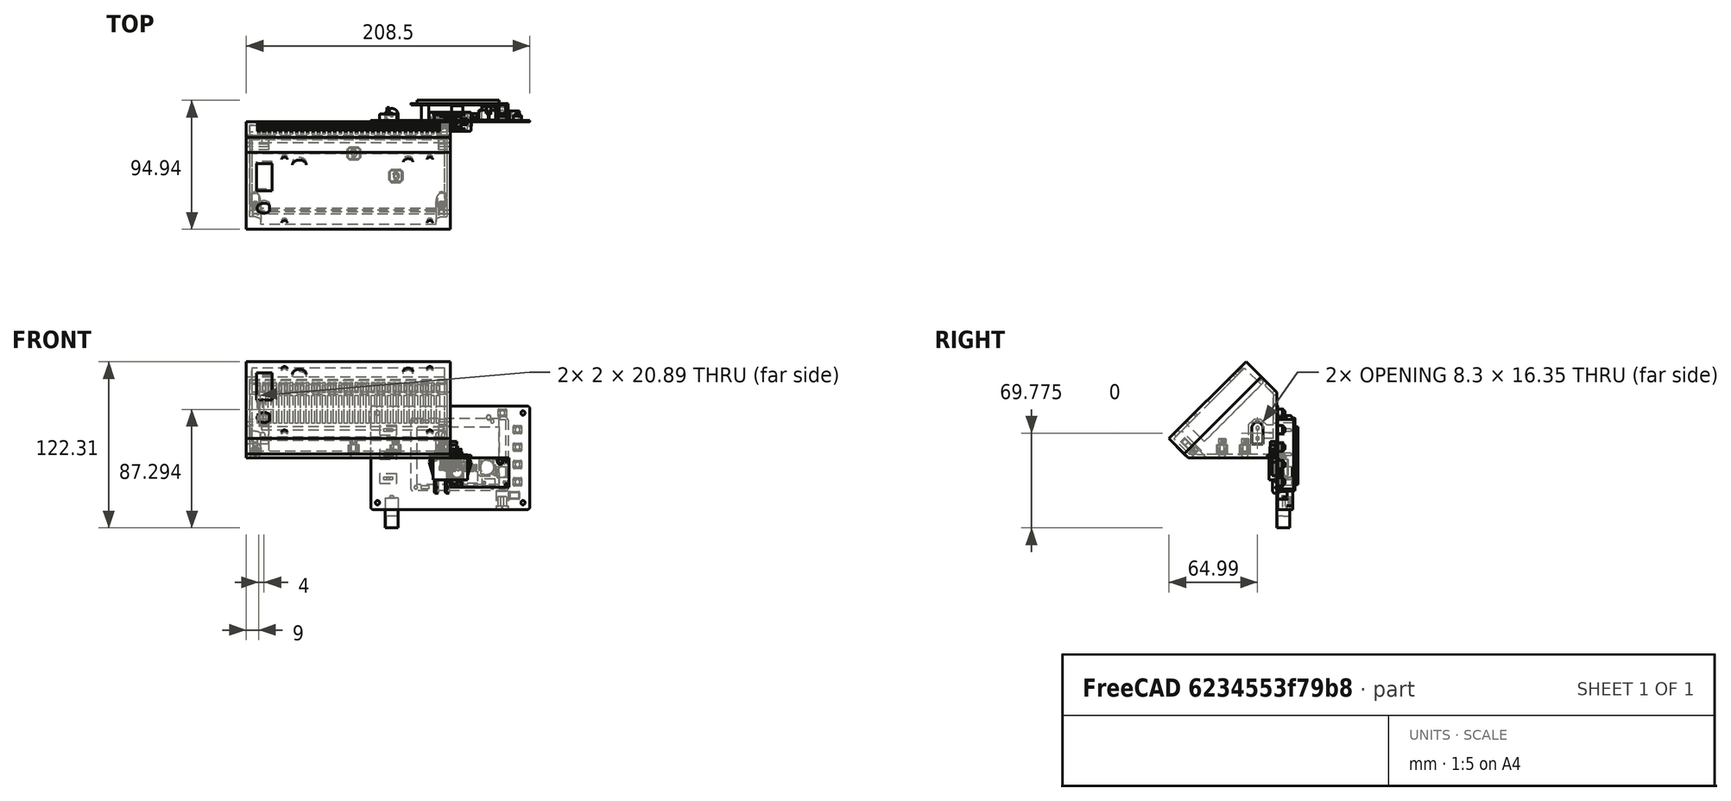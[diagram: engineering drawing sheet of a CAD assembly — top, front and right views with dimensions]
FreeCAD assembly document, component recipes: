
FREECAD ASSEMBLY — COMPONENT RECIPES ("oscillo_009_surBase35mm_007.5")

This assembly document has 19 components, labeled P0..P18 below (a component is one placed body or linked part). 12 of them carry a construction recipe — the FreeCAD feature program that regenerates the part from scratch, quoted from this document or its linked companion documents; the rest are supplied as boundary geometry only. No exploded tour is included for this assembly.
COMPONENT P0 — recipe-attached ("base", modeled in this document).
Construction recipe (the document's own serialized feature program — sketch geometry with constraints, then the solid features built on it; lengths are millimeters unless a unit is written):

FEATURE [PartDesign::FeatureBase] Clone
  BaseFeature = -> Slice_child0
FEATURE [PartDesign::Thickness] Thickness
  Base = -> Clone [Face7]
  BaseFeature = -> Clone
  Intersection = false
  Join = 0
  Mode = 0
  Reversed = true
  SupportTransform = false
  Value = 2.5
  expr: Value = <<sp>>.epaisseurParois
FEATURE [PartDesign::Plane] DatumPlane001  label="planXt"
  AttachmentOffset = pos=(0,0,-2.5) rot=(0,0,1;0rad)
  Length = 110.737
  MapMode = 5
  Placement = pos=(-2.5,6e-16,-6e-16) rot=(0.57735,0.57735,0.57735;2.0944rad)
  ResizeMode = 0
  Support = -> [YZ_Plane002]
  Width = 102.305
  expr: .AttachmentOffset.Base.z = -<<sp>>.epaisseurParois
FEATURE [Sketcher::SketchObject] Sketch002  label="sk_renfortXt"
  FullyConstrained = true
  MapMode = 5
  Placement = pos=(-2.5,6e-16,-6e-16) rot=(0.57735,0.57735,0.57735;2.0944rad)
  Support = -> [DatumPlane001]
  expr: .Constraints.dist = <<sp>>.xt60distanceAngleBord
  expr: .Constraints.epRf = <<sp>>.xt60epRenfort
  expr: Constraints[13] = <<sp>>.xt60largeurFetiere
  expr: Constraints[14] = <<sp>>.xt60hauteur
  expr: Constraints[15] = <<sp>>.xt60hauteurToit
  expr: Constraints[16] = <<sp>>.xt60base
  expr: Constraints[18] = .Constraints.dist
  expr: Constraints[31] = <<sp>>.epaisseurParois
  expr: Constraints[32] = .Constraints.epRf
  expr: Constraints[34] = .Constraints.epRf
  expr: Constraints[45] = <<sp>>.epaisseurParois
  sketch-geometry (17):
    g0: LineSegment StartX=-18.3 StartY=10 StartZ=0 EndX=-18.3 EndY=23.25 EndZ=0
    g1: LineSegment StartX=-18.3 StartY=23.25 StartZ=0 EndX=-15.65 EndY=25.75 EndZ=0
    g2: LineSegment StartX=-15.65 StartY=25.75 StartZ=0 EndX=-12.65 EndY=25.75 EndZ=0
    g3: LineSegment StartX=-12.65 StartY=25.75 StartZ=0 EndX=-10 EndY=23.25 EndZ=0
    g4: LineSegment StartX=-10 StartY=23.25 StartZ=0 EndX=-10 EndY=10 EndZ=0
    g5: LineSegment StartX=-10 StartY=10 StartZ=0 EndX=-18.3 EndY=10 EndZ=0
    g6: LineSegment StartX=-14.15 StartY=10 StartZ=0 EndX=-14.15 EndY=25.75 EndZ=0
    g7: LineSegment StartX=-16.6431 StartY=28.25 StartZ=0 EndX=-20.8 EndY=24.3284 EndZ=0
    g8: LineSegment StartX=-20.8 StartY=24.3284 StartZ=0 EndX=-20.8 EndY=2.5 EndZ=0
    g9: LineSegment StartX=-20.8 StartY=2.5 StartZ=0 EndX=-7.5 EndY=2.5 EndZ=0
    g10: LineSegment StartX=-7.5 StartY=2.5 StartZ=0 EndX=-7.5 EndY=24.3284 EndZ=0
    g11: LineSegment StartX=-7.5 StartY=24.3284 StartZ=0 EndX=-11.6569 EndY=28.25 EndZ=0
    g12: LineSegment StartX=-11.6569 StartY=28.25 StartZ=0 EndX=-16.6431 EndY=28.25 EndZ=0
    g13: LineSegment StartX=-7.5 StartY=24.3284 StartZ=0 EndX=-2.5 EndY=24.3284 EndZ=0
    g14: LineSegment StartX=-2.5 StartY=24.3284 StartZ=0 EndX=-2.5 EndY=2.5 EndZ=0
    g15: LineSegment StartX=-2.5 StartY=2.5 StartZ=0 EndX=-7.5 EndY=2.5 EndZ=0
    g16: LineSegment StartX=-7.5 StartY=2.5 StartZ=0 EndX=-7.5 EndY=24.3284 EndZ=0
  constraints (46):
    c: Vertical(g0)
    c: Coincident(g0,g1)
    c: Coincident(g1,g2)
    c: Horizontal(g2)
    c: Coincident(g2,g3)
    c: Coincident(g3,g4)
    c: Vertical(g4)
    c: Coincident(g4,g5)
    c: Coincident(g5,g0)
    c: Horizontal(g5)
    c: Symmetric(g1,g2,g6)
    c: Equal(g0,g4)
    c: Symmetric(g0,g4,g6)
    c: DistanceX(g2,g2) = 3
    c: DistanceY(g4,g4) = 13.25
    c: DistanceY(g3,g2) = 2.5
    c: DistanceX(g5,g5) = 8.3
    c: DistanceX(g4,g-1) = 10  'dist'
    c: DistanceY(g-1,g4) = 10
    c: Coincident(g7,g8)
    c: Vertical(g8)
    c: Coincident(g8,g9)
    c: Horizontal(g9)
    c: Coincident(g9,g10)
    c: Coincident(g10,g11)
    c: Coincident(g11,g12)
    c: Coincident(g12,g7)
    c: Symmetric(g7,g10,g6)
    c: Symmetric(g7,g11,g6)
    c: Symmetric(g8,g9,g6)
    c: DistanceX(g8,g0) = 2.5  'epRf'
    c: DistanceY(g-1,g9) = 2.5
    c: Distance(g7,g1) = 2.5
    c: Parallel(g1,g7)
    c: DistanceY(g2,g11) = 2.5
    c: Coincident(g13,g14)
    c: Coincident(g14,g15)
    c: Coincident(g15,g16)
    c: Coincident(g16,g13)
    c: Horizontal(g13)
    c: Horizontal(g15)
    c: Vertical(g14)
    c: Vertical(g16)
    c: Coincident(g13,g11)
    c: Horizontal(g14,g9)
    c: DistanceX(g14,g-1) = 2.5
FEATURE [PartDesign::Pad] Pad001  label="renfortXt"
  AllowMultiFace = false
  BaseFeature = -> Thickness
  Direction = (1,1,1)
  Length = 145
  Length2 = 100
  Profile = -> Sketch002
  Reversed = true
  Type = 0
  expr: Length = <<sp>>.largeurModuleBase - 2 * <<sp>>.epaisseurParois
FEATURE [Sketcher::SketchObject] Sketch003  label="sk_trouXt"
  FullyConstrained = true
  MapMode = 5
  Placement = pos=(0,0,0) rot=(0.57735,0.57735,0.57735;2.0944rad)
  Support = -> [YZ_Plane002]
  expr: .Constraints.dist = <<sp>>.xt60distanceAngleBord
  expr: Constraints[13] = <<sp>>.xt60base
  expr: Constraints[14] = <<sp>>.xt60hauteur
  expr: Constraints[15] = <<sp>>.xt60hauteurToit + <<sp>>.xtJeu
  expr: Constraints[16] = <<sp>>.xt60largeurFetiere
  expr: Constraints[18] = .Constraints.dist
  sketch-geometry (7):
    g0: LineSegment StartX=-18.3 StartY=10 StartZ=0 EndX=-18.3 EndY=23.25 EndZ=0
    g1: LineSegment StartX=-18.3 StartY=23.25 StartZ=0 EndX=-15.65 EndY=26.35 EndZ=0
    g2: LineSegment StartX=-15.65 StartY=26.35 StartZ=0 EndX=-12.65 EndY=26.35 EndZ=0
    g3: LineSegment StartX=-12.65 StartY=26.35 StartZ=0 EndX=-10 EndY=23.25 EndZ=0
    g4: LineSegment StartX=-10 StartY=23.25 StartZ=0 EndX=-10 EndY=10 EndZ=0
    g5: LineSegment StartX=-10 StartY=10 StartZ=0 EndX=-18.3 EndY=10 EndZ=0
    g6: LineSegment StartX=-14.15 StartY=10 StartZ=0 EndX=-14.15 EndY=26.35 EndZ=0
  constraints (19):
    c: Vertical(g0)
    c: Coincident(g0,g1)
    c: Coincident(g1,g2)
    c: Horizontal(g2)
    c: Coincident(g2,g3)
    c: Coincident(g3,g4)
    c: Coincident(g4,g5)
    c: Coincident(g5,g0)
    c: Horizontal(g5)
    c: Symmetric(g1,g2,g6)
    c: Symmetric(g0,g3,g6)
    c: Vertical(g6)
    c: Symmetric(g0,g4,g6)
    c: DistanceX(g5,g5) = 8.3
    c: DistanceY(g4,g4) = 13.25
    c: DistanceY(g3,g2) = 3.1
    c: DistanceX(g2,g2) = 3
    c: DistanceX(g4,g-1) = 10  'dist'
    c: DistanceY(g-1,g4) = 10
FEATURE [PartDesign::Pocket] Pocket
  AllowMultiFace = false
  BaseFeature = -> Pad001
  Direction = (1,1,1)
  Length = 150
  Length2 = 100
  Profile = -> Sketch003
  Type = 0
  expr: Length = <<sp>>.largeurModuleBase
FEATURE [PartDesign::Plane] DatumPlane002  label="planDecoupeRenfortXt"
  AttachmentOffset = pos=(0,0,2.5) rot=(0,0,1;0rad)
  Length = 199.331
  MapMode = 5
  Placement = pos=(0,-2.5,-6e-16) rot=(1,0,0;1.5708rad)
  ResizeMode = 0
  Support = -> [XZ_Plane002]
  Width = 108.899
  expr: .AttachmentOffset.Base.z = <<sp>>.epaisseurParois
FEATURE [Sketcher::SketchObject] Sketch004  label="sk_decoupRenfXt"
  FullyConstrained = true
  MapMode = 5
  Placement = pos=(0,-2.5,-6e-16) rot=(1,0,0;1.5708rad)
  Support = -> [DatumPlane002]
  expr: Constraints[10] = <<sp>>.xt60LongueurRenfortPetit + <<sp>>.epaisseurParois
  expr: Constraints[11] = <<sp>>.largeurModuleBase - (<<sp>>.xt60longueurRenfortGrand + <<sp>>.epaisseurParois)
  expr: Constraints[8] = <<sp>>.epaisseurParois
  expr: Constraints[9] = <<sp>>.xt60distanceAngleBord + <<sp>>.xt60hauteur + <<sp>>.xt60hauteurToit + <<sp>>.xt60epRenfort
  sketch-geometry (4):
    g0: LineSegment StartX=-133.5 StartY=28.25 StartZ=0 EndX=-8.5 EndY=28.25 EndZ=0
    g1: LineSegment StartX=-8.5 StartY=28.25 StartZ=0 EndX=-8.5 EndY=2.5 EndZ=0
    g2: LineSegment StartX=-8.5 StartY=2.5 StartZ=0 EndX=-133.5 EndY=2.5 EndZ=0
    g3: LineSegment StartX=-133.5 StartY=2.5 StartZ=0 EndX=-133.5 EndY=28.25 EndZ=0
  constraints (12):
    c: Coincident(g0,g1)
    c: Coincident(g1,g2)
    c: Coincident(g2,g3)
    c: Coincident(g3,g0)
    c: Horizontal(g0)
    c: Horizontal(g2)
    c: Vertical(g1)
    c: Vertical(g3)
    c: DistanceY(g-1,g1) = 2.5
    c: DistanceY(g-1,g0) = 28.25
    c: DistanceX(g1,g-1) = 8.5
    c: DistanceX(g2,g-1) = 133.5
FEATURE [PartDesign::Pocket] Pocket001  label="decoupeRenfXt"
  AllowMultiFace = false
  BaseFeature = -> Pocket
  Direction = (1,1,1)
  Length = 23.3
  Length2 = 100
  Profile = -> Sketch004
  Reversed = true
  Type = 0
  expr: Length = <<sp>>.xt60distanceAngleBord + <<sp>>.xt60base + 2 * <<sp>>.xt60epRenfort
FEATURE [Sketcher::SketchObject] Sketch005  label="xt60PercagePostMale"
  FullyConstrained = true
  MapMode = 5
  Placement = pos=(0,0,0) rot=(1,0,0;1.5708rad)
  Support = -> [XZ_Plane002]
  expr: Constraints[0] = <<sp>>.insertDiamPercage
  expr: Constraints[1] = <<sp>>.insertDistanceTrouBordMale
  expr: Constraints[2] = <<sp>>.insertHauteur
  sketch-geometry (1):
    g0: Circle CenterX=-4.5 CenterY=16.625 CenterZ=0 NormalX=0 NormalY=0 NormalZ=1 AngleXU=0 Radius=2
  constraints (3):
    c: Diameter(g0) = 4
    c: DistanceX(g0,g-1) = 4.5
    c: DistanceY(g-1,g0) = 16.625
FEATURE [PartDesign::Pocket] Pocket002  label="insertXtMale"
  AllowMultiFace = false
  BaseFeature = -> Pocket001
  Direction = (1,1,1)
  Length = 10
  Length2 = 100
  Profile = -> Sketch005
  Reversed = true
  Type = 0
  expr: Length = <<sp>>.insertProfondeurPercage
FEATURE [Sketcher::SketchObject] Sketch006  label="xt60PercagePostFem"
  FullyConstrained = true
  MapMode = 5
  Placement = pos=(0,0,0) rot=(1,0,0;1.5708rad)
  Support = -> [XZ_Plane002]
  expr: Constraints[0] = <<sp>>.insertDiamPercage
  expr: Constraints[1] = <<sp>>.insertDistanceTrouBordFem
  expr: Constraints[2] = <<sp>>.insertHauteur
  sketch-geometry (1):
    g0: Circle CenterX=-138 CenterY=16.625 CenterZ=0 NormalX=0 NormalY=0 NormalZ=1 AngleXU=0 Radius=2
  constraints (3):
    c: Diameter(g0) = 4
    c: DistanceX(g0,g-1) = 138
    c: DistanceY(g-1,g0) = 16.625
FEATURE [PartDesign::Pocket] Pocket003  label="insertXt60Fem"
  AllowMultiFace = false
  BaseFeature = -> Pocket002
  Direction = (1,1,1)
  Length = 10
  Length2 = 100
  Profile = -> Sketch006
  Reversed = true
  Type = 0
  expr: Length = <<sp>>.insertProfondeurPercage
FEATURE [PartDesign::Plane] DatumPlane003
  AttachmentOffset = pos=(0,0,2.5) rot=(0,0,1;0rad)
  Length = 200.515
  MapMode = 2
  Placement = pos=(0,0,2.5) rot=(0,0,1;0rad)
  ResizeMode = 0
  Support = -> [XY_Plane002]
  Width = 118.515
  expr: .AttachmentOffset.Base.z = <<sp>>.epaisseurParois
FEATURE [PartDesign::Plane] DatumPlane004  label="planTrancheur"
  AttachmentOffset = pos=(0,0,71) rot=(-1,0,0;0.785398rad)
  Length = 204.647
  MapMode = 5
  Placement = pos=(0,-71,-1.58e-14) rot=(1,0,0;0.785398rad)
  ResizeMode = 0
  Support = -> [XZ_Plane002]
  Width = 155.206
  expr: .AttachmentOffset.Base.z = <<sp>>.planTrancheur
FEATURE [Sketcher::SketchObject] Sketch008
  FullyConstrained = true
  MapMode = 5
  Placement = pos=(0,-71,-2.13e-14) rot=(1,0,0;0.785398rad)
  Support = -> [DatumPlane004]
  expr: .Constraints.dist = <<sp>>.epaisseurParois
  expr: Constraints[13] = <<sp>>.epaisseurParois
  expr: Constraints[16] = <<sp>>.insertDiamPercage / 2 + <<sp>>.insertFAVMargeDist
  expr: Constraints[1] = <<sp>>.insertFavDistAuZeroDuPLan
  expr: Constraints[21] = <<sp>>.insertFAVDistBord
  expr: Constraints[22] = <<sp>>.largeurModuleBase - <<sp>>.epaisseurParois
  sketch-geometry (7):
    g0: LineSegment StartX=-2.5 StartY=4.24264 StartZ=0 EndX=-147.5 EndY=4.24264 EndZ=0
    g1: LineSegment StartX=-6.5 StartY=14.7426 StartZ=0 EndX=-2.5 EndY=14.7426 EndZ=0
    g2: LineSegment StartX=-2.5 StartY=14.7426 StartZ=0 EndX=-2.5 EndY=6.74264 EndZ=0
    g3: LineSegment StartX=-2.5 StartY=6.74264 StartZ=0 EndX=-10.5 EndY=6.74264 EndZ=0
    g4: LineSegment StartX=-10.5 StartY=6.74264 StartZ=0 EndX=-10.5 EndY=10.7426 EndZ=0
    g5: ArcOfCircle CenterX=-6.5 CenterY=10.7426 CenterZ=0 NormalX=0 NormalY=0 NormalZ=1 AngleXU=0 Radius=4 StartAngle=1.5708 EndAngle=3.14159
    g6: LineSegment StartX=-6.5 StartY=10.7426 StartZ=0 EndX=-6.5 EndY=6.74264 EndZ=0
  constraints (23):
    c: Horizontal(g0)
    c: DistanceY(g-1,g0) = 4.24264
    c: DistanceX(g0,g-1) = 2.5  'dist'
    c: Horizontal(g1)
    c: Coincident(g1,g2)
    c: Vertical(g2)
    c: Coincident(g2,g3)
    c: Horizontal(g3)
    c: Coincident(g3,g4)
    c: Vertical(g4)
    c: Vertical(g2,g0)
    c: Equal(g3,g2)
    c: Equal(g4,g1)
    c: DistanceY(g0,g2) = 2.5
    c: Coincident(g5,g4)
    c: Coincident(g5,g1)
    c: DistanceX(g5,g2) = 4
    c: Coincident(g6,g5)
    c: PointOnObject(g6,g3)
    c: Vertical(g6)
    c: Vertical(g5,g1)
    c: DistanceX(g3,g3) = 8
    c: DistanceX(g0,g-1) = 147.5
FEATURE [PartDesign::Pad] Pad003  label="padTrouFAVDroite"
  AllowMultiFace = false
  BaseFeature = -> Pocket003
  Direction = (1,1,1)
  Length = 10
  Length2 = 100
  Profile = -> Sketch008
  Reversed = true
  Type = 3
  UpToFace = -> DatumPlane003
FEATURE [Sketcher::SketchObject] Sketch009
  FullyConstrained = true
  MapMode = 5
  Placement = pos=(0,-71,-2.13e-14) rot=(1,0,0;0.785398rad)
  Support = -> [DatumPlane004]
  expr: .Constraints.larg = <<sp>>.insertFAVDistBord
  expr: Constraints[11] = .Constraints.larg / 2
  expr: Constraints[12] = <<sp>>.largeurModuleBase
  expr: Constraints[13] = <<sp>>.insertFavDistAuZeroDuPLan
  expr: Constraints[14] = <<sp>>.epaisseurParois
  expr: Constraints[15] = <<sp>>.epaisseurParois
  expr: Constraints[8] = .Constraints.larg
  sketch-geometry (6):
    g0: LineSegment StartX=-147.5 StartY=6.74264 StartZ=0 EndX=-139.5 EndY=6.74264 EndZ=0
    g1: LineSegment StartX=-139.5 StartY=6.74264 StartZ=0 EndX=-139.5 EndY=10.7426 EndZ=0
    g2: LineSegment StartX=-143.5 StartY=14.7426 StartZ=0 EndX=-147.5 EndY=14.7426 EndZ=0
    g3: LineSegment StartX=-147.5 StartY=14.7426 StartZ=0 EndX=-147.5 EndY=6.74264 EndZ=0
    g4: ArcOfCircle CenterX=-143.5 CenterY=10.7426 CenterZ=0 NormalX=0 NormalY=0 NormalZ=1 AngleXU=0 Radius=4 StartAngle=0 EndAngle=1.5708
    g5: GeomPoint X=-150 Y=4.24264 Z=0
  constraints (16):
    c: Coincident(g0,g1)
    c: Coincident(g2,g3)
    c: Coincident(g3,g0)
    c: Horizontal(g0)
    c: Horizontal(g2)
    c: Vertical(g1)
    c: Vertical(g3)
    c: DistanceX(g0,g0) = 8  'larg'
    c: DistanceY(g3,g3) = 8
    c: Tangent(g2,g4) = -1.5708
    c: Tangent(g1,g4) = -1.5708
    c: DistanceX(g0,g4) = 4
    c: DistanceX(g5,g-1) = 150
    c: DistanceY(g-1,g5) = 4.24264
    c: DistanceX(g5,g0) = 2.5
    c: DistanceY(g5,g0) = 2.5
FEATURE [PartDesign::Pad] Pad004  label="padTrouFavGauche"
  AllowMultiFace = false
  BaseFeature = -> Pad003
  Direction = (1,1,1)
  Length = 10
  Length2 = 100
  Profile = -> Sketch009
  Type = 3
  UpToFace = -> DatumPlane003 [Plane]
FEATURE [Sketcher::SketchObject] Sketch010
  FullyConstrained = true
  MapMode = 5
  Placement = pos=(0,-71,-2.13e-14) rot=(1,0,0;0.785398rad)
  Support = -> [DatumPlane004]
  expr: Constraints[0] = <<sp>>.insertFAVDistBord / 2 + <<sp>>.epaisseurParois
  expr: Constraints[1] = <<sp>>.insertFavDistAuZeroDuPLan + <<sp>>.epaisseurParois + <<sp>>.insertFAVDistBord / 2
  expr: Constraints[2] = <<sp>>.insertDiamPercage
  sketch-geometry (1):
    g0: Circle CenterX=-6.5 CenterY=10.7426 CenterZ=0 NormalX=0 NormalY=0 NormalZ=1 AngleXU=0 Radius=2
  constraints (3):
    c: DistanceX(g0,g-1) = 6.5
    c: DistanceY(g-1,g0) = 10.7426
    c: Diameter(g0) = 4
FEATURE [PartDesign::Pocket] Pocket004  label="trouDroit"
  AllowMultiFace = false
  BaseFeature = -> Pad004
  Direction = (1,1,1)
  Length = 5
  Length2 = 100
  Profile = -> Sketch010
  Type = 1
FEATURE [Sketcher::SketchObject] Sketch011
  FullyConstrained = true
  MapMode = 5
  Placement = pos=(0,-71,-2.13e-14) rot=(1,0,0;0.785398rad)
  Support = -> [DatumPlane004]
  expr: Constraints[0] = <<sp>>.insertDiamPercage
  expr: Constraints[1] = <<sp>>.largeurModuleBase - <<sp>>.epaisseurParois - <<sp>>.insertFAVDistBord / 2
  expr: Constraints[2] = <<sp>>.insertFavDistAuZeroDuPLan + <<sp>>.epaisseurParois + <<sp>>.insertFAVDistBord / 2
  sketch-geometry (1):
    g0: Circle CenterX=-143.5 CenterY=10.7426 CenterZ=0 NormalX=0 NormalY=0 NormalZ=1 AngleXU=0 Radius=2
  constraints (3):
    c: Diameter(g0) = 4
    c: DistanceX(g0,g-1) = 143.5
    c: DistanceY(g-1,g0) = 10.7426
FEATURE [PartDesign::Pocket] Pocket005  label="trouGauche"
  AllowMultiFace = false
  BaseFeature = -> Pocket004
  Direction = (1,1,1)
  Length = 5
  Length2 = 100
  Profile = -> Sketch011
  Type = 1
FEATURE [PartDesign::Plane] DatumPlane005  label="planTeteVisFav"
  AttachmentOffset = pos=(0,0,68) rot=(-1,0,0;0.785398rad)
  Length = 204.647
  MapMode = 5
  Placement = pos=(0,-68,-1.51e-14) rot=(1,0,0;0.785398rad)
  ResizeMode = 0
  Support = -> [XZ_Plane002]
  Width = 155.206
  expr: .AttachmentOffset.Base.z = <<sp>>.planTrancheur - 3
FEATURE [Sketcher::SketchObject] Sketch012
  ExternalGeometry = -> [Pocket005]
  FullyConstrained = true
  MapMode = 5
  Placement = pos=(0,-68,-1.42e-14) rot=(1,0,0;0.785398rad)
  Support = -> [DatumPlane005]
  expr: Constraints[1] = <<sp>>.visM3DiamEncastrement
  sketch-geometry (2):
    g0: Circle CenterX=-6.5 CenterY=8.62132 CenterZ=0 NormalX=0 NormalY=0 NormalZ=1 AngleXU=0 Radius=3
    g1: Circle CenterX=-143.5 CenterY=8.62132 CenterZ=0 NormalX=0 NormalY=0 NormalZ=1 AngleXU=0 Radius=3
  constraints (4):
    c: Equal(g0,g1)
    c: Diameter(g1) = 6
    c: Coincident(g1,g-4)
    c: Coincident(g-3,g0)
FEATURE [PartDesign::Pocket] Pocket006  label="evidementTeteVisFav"
  AllowMultiFace = false
  BaseFeature = -> Pocket005
  Direction = (1,1,1)
  Length = 20
  Length2 = 100
  Profile = -> Sketch012
  Type = 1
FEATURE [Sketcher::SketchObject] Sketch014
  FullyConstrained = true
  MapMode = 5
  Placement = pos=(0,0,0) rot=(1,0,0;1.5708rad)
  Support = -> [XZ_Plane002]
  expr: Constraints[12] = <<sp>>.xt60distanceAngleBord + <<sp>>.xt60hauteur + <<sp>>.ventilDistBordFente
  expr: Constraints[13] = <<sp>>.ventilLargeurFentes
  expr: Constraints[14] = <<sp>>.ventilEcartfente / 2
  expr: Constraints[15] = <<sp>>.hauteurDuDos - <<sp>>.ventilDistBordFente
  expr: Constraints[2] = <<sp>>.hauteurDuDos
  expr: Constraints[3] = <<sp>>.largeurModuleBase / 2
  sketch-geometry (5):
    g0: LineSegment StartX=-75 StartY=0 StartZ=0 EndX=-75 EndY=48.1371 EndZ=0
    g1: LineSegment StartX=-78 StartY=46.1371 StartZ=0 EndX=-76 EndY=46.1371 EndZ=0
    g2: LineSegment StartX=-76 StartY=46.1371 StartZ=0 EndX=-76 EndY=25.25 EndZ=0
    g3: LineSegment StartX=-76 StartY=25.25 StartZ=0 EndX=-78 EndY=25.25 EndZ=0
    g4: LineSegment StartX=-78 StartY=25.25 StartZ=0 EndX=-78 EndY=46.1371 EndZ=0
  constraints (16):
    c: PointOnObject(g0,g-1)
    c: Vertical(g0)
    c: DistanceY(g0,g0) = 48.1371
    c: DistanceX(g0,g-1) = 75
    c: Coincident(g1,g2)
    c: Coincident(g2,g3)
    c: Coincident(g3,g4)
    c: Coincident(g4,g1)
    c: Horizontal(g1)
    c: Horizontal(g3)
    c: Vertical(g2)
    c: Vertical(g4)
    c: DistanceY(g-1,g2) = 25.25
    c: DistanceX(g1,g1) = 2
    c: DistanceX(g2,g0) = 1
    c: DistanceY(g-1,g1) = 46.1371
FEATURE [PartDesign::Pocket] Pocket008  label="ventilFente1"
  AllowMultiFace = false
  BaseFeature = -> Pocket006
  Direction = (1,1,1)
  Length = 2.5
  Length2 = 100
  Profile = -> Sketch014
  Reversed = true
  Type = 0
  expr: Length = <<sp>>.epaisseurParois
FEATURE [PartDesign::LinearPattern] LinearPattern  label="ventilDosRepeat1"
  BaseFeature = -> Pocket008
  Direction = -> Sketch014 [H_Axis]
  Length = 64
  Occurrences = 17
  Originals = -> [Pocket008]
  Reversed = true
  expr: Length = <<sp>>.ventilLargeurRepet
  expr: Occurrences = <<sp>>.ventilNbrFents
FEATURE [PartDesign::LinearPattern] LinearPattern001  label="ventilDosRepeat2"
  BaseFeature = -> LinearPattern
  Direction = -> Sketch014 [H_Axis]
  Length = 68
  Occurrences = 18
  Originals = -> [Pocket008]
  expr: Length = <<sp>>.ventilLargeurRepet + <<sp>>.ventilEcartfente + <<sp>>.ventilLargeurFentes
  expr: Occurrences = <<sp>>.ventilNbrFents + 1
FEATURE [PartDesign::Plane] DatumPlane006  label="planVentilSup"
  AttachmentOffset = pos=(0,0,-48.1371) rot=(1,0,0;0.785398rad)
  Length = 204.647
  MapMode = 5
  Placement = pos=(0,48.1371,1.07e-14) rot=(1,0,0;2.35619rad)
  ResizeMode = 0
  Support = -> [XZ_Plane002]
  Width = 155.206
  expr: .AttachmentOffset.Base.z = -<<sp>>.hauteurDuDos
FEATURE [Sketcher::SketchObject] Sketch015
  FullyConstrained = true
  MapMode = 5
  Placement = pos=(0,48.1371,1.07e-14) rot=(1,0,0;2.35619rad)
  Support = -> [DatumPlane006]
  expr: Constraints[10] = <<sp>>.ventilLargeurFentes
  expr: Constraints[11] = (<<sp>>.largeurModuleBase + <<sp>>.ventilEcartfente) / 2
  expr: Constraints[8] = <<sp>>.distanceAuZeroPlanBorArriere + <<sp>>.ventilDistBordFente
  expr: Constraints[9] = <<sp>>.longPetitRetSupSansFav - 2 * <<sp>>.ventilDistBordFente - <<sp>>.favBordureProf
  sketch-geometry (4):
    g0: LineSegment StartX=-76 StartY=78.0926 StartZ=0 EndX=-78 EndY=78.0926 EndZ=0
    g1: LineSegment StartX=-78 StartY=78.0926 StartZ=0 EndX=-78 EndY=70.0761 EndZ=0
    g2: LineSegment StartX=-78 StartY=70.0761 StartZ=0 EndX=-76 EndY=70.0761 EndZ=0
    g3: LineSegment StartX=-76 StartY=70.0761 StartZ=0 EndX=-76 EndY=78.0926 EndZ=0
  constraints (12):
    c: Coincident(g0,g1)
    c: Coincident(g1,g2)
    c: Coincident(g2,g3)
    c: Coincident(g3,g0)
    c: Horizontal(g0)
    c: Horizontal(g2)
    c: Vertical(g1)
    c: Vertical(g3)
    c: DistanceY(g-1,g2) = 70.0761
    c: DistanceY(g2,g0) = 8.01652
    c: DistanceX(g0,g0) = 2
    c: DistanceX(g2,g-1) = 76
FEATURE [PartDesign::Pocket] Pocket009  label="ventilSupFente"
  AllowMultiFace = false
  BaseFeature = -> LinearPattern001
  Direction = (1,1,1)
  Length = 5
  Length2 = 100
  Profile = -> Sketch015
  Reversed = true
  Type = 0
FEATURE [PartDesign::LinearPattern] LinearPattern002  label="ventilSupRepeat1"
  BaseFeature = -> Pocket009
  Direction = -> Sketch015 [H_Axis]
  Length = 64
  Occurrences = 17
  Originals = -> [Pocket009]
  Reversed = true
  expr: Length = <<sp>>.ventilLargeurRepet
  expr: Occurrences = <<sp>>.ventilNbrFents
FEATURE [PartDesign::LinearPattern] LinearPattern003  label="ventilSupRepeat2"
  BaseFeature = -> LinearPattern002
  Direction = -> Sketch015 [H_Axis]
  Length = 68
  Occurrences = 18
  Originals = -> [Pocket009]
  expr: Length = <<sp>>.ventilLargeurRepet + <<sp>>.ventilEcartfente + <<sp>>.ventilLargeurFentes
  expr: Occurrences = <<sp>>.ventilNbrFents + 1
FEATURE [PartDesign::Body] Body001  label="base"
  BaseFeature = -> Slice_child0
  Group = -> [Clone,Thickness,DatumPlane001,Sketch002,Pad001,Sketch003,Pocket,DatumPlane002,Sketch004,Pocket001,Sketch005,Pocket002,Sketch006,Pocket003,DatumPlane003,DatumPlane004,Sketch008,Pad003,Sketch009,Pad004,Sketch010,Pocket004,Sketch011,Pocket005,DatumPlane005,Sketch012,Pocket006,Sketch014,Pocket008,LinearPattern,LinearPattern001,DatumPlane006,Sketch015,Pocket009,LinearPattern002,LinearPattern003,+10 more]
  Origin = -> Origin002
  Tip = -> Chamfer005
COMPONENT P1 — recipe-attached ("faceAvant", modeled in this document).
Construction recipe (the document's own serialized feature program — sketch geometry with constraints, then the solid features built on it; lengths are millimeters unless a unit is written):

FEATURE [PartDesign::FeatureBase] Clone001
  BaseFeature = -> Slice_child1
FEATURE [PartDesign::Thickness] Thickness001
  Base = -> Clone001 [Face5]
  BaseFeature = -> Clone001
  Intersection = false
  Join = 0
  Mode = 0
  Reversed = true
  SupportTransform = false
  Value = 2.5
  expr: Value = <<sp>>.epaisseurParois
FEATURE [PartDesign::Plane] DatumPlane007  label="planTrancheurBis"
  AttachmentOffset = pos=(0,0,71) rot=(-1,0,0;0.785398rad)
  Length = 206.452
  MapMode = 5
  Placement = pos=(0,-71,-1.58e-14) rot=(1,0,0;0.785398rad)
  ResizeMode = 0
  Support = -> [XZ_Plane003]
  Width = 172.769
  expr: .AttachmentOffset.Base.z = <<sp>>.planTrancheur
FEATURE [Sketcher::SketchObject] Sketch016  label="sk_insertFavDroit"
  FullyConstrained = true
  MapMode = 5
  Placement = pos=(0,-71,-2.13e-14) rot=(1,0,0;0.785398rad)
  Support = -> [DatumPlane007]
  expr: Constraints[11] = <<sp>>.insertFAVDistBord
  expr: Constraints[14] = <<sp>>.insertFAVDistBord / 2
  expr: Constraints[7] = <<sp>>.epaisseurParois
  expr: Constraints[8] = <<sp>>.insertFavDistAuZeroDuPLan + <<sp>>.epaisseurParois
  expr: Constraints[9] = <<sp>>.insertFAVDistBord
  sketch-geometry (5):
    g0: LineSegment StartX=-6.5 StartY=14.7426 StartZ=0 EndX=-2.5 EndY=14.7426 EndZ=0
    g1: LineSegment StartX=-2.5 StartY=14.7426 StartZ=0 EndX=-2.5 EndY=6.74264 EndZ=0
    g2: LineSegment StartX=-2.5 StartY=6.74264 StartZ=0 EndX=-10.5 EndY=6.74264 EndZ=0
    g3: LineSegment StartX=-10.5 StartY=6.74264 StartZ=0 EndX=-10.5 EndY=10.7426 EndZ=0
    g4: ArcOfCircle CenterX=-6.5 CenterY=10.7426 CenterZ=0 NormalX=0 NormalY=0 NormalZ=1 AngleXU=0 Radius=4 StartAngle=1.5708 EndAngle=3.14159
  constraints (15):
    c: Horizontal(g0)
    c: Coincident(g0,g1)
    c: Vertical(g1)
    c: Coincident(g1,g2)
    c: Horizontal(g2)
    c: Coincident(g2,g3)
    c: Vertical(g3)
    c: DistanceX(g1,g-1) = 2.5
    c: DistanceY(g-1,g1) = 6.74264
    c: DistanceY(g1,g1) = 8
    c: Equal(g3,g0)
    c: DistanceX(g2,g2) = 8
    c: Coincident(g4,g0)
    c: Tangent(g4,g3) = 1.5708
    c: DistanceX(g4,g1) = 4
FEATURE [PartDesign::Pad] Pad005  label="padInsertFavDroit"
  AllowMultiFace = false
  BaseFeature = -> Thickness001
  Direction = (1,1,1)
  Length = 10
  Length2 = 100
  Profile = -> Sketch016
  Type = 2
FEATURE [Sketcher::SketchObject] Sketch017  label="sp_padInserFavGauch"
  FullyConstrained = true
  MapMode = 5
  Placement = pos=(0,-71,-2.13e-14) rot=(1,0,0;0.785398rad)
  Support = -> [DatumPlane007]
  expr: Constraints[10] = <<sp>>.insertFAVDistBord
  expr: Constraints[12] = <<sp>>.insertFAVDistBord / 2
  expr: Constraints[13] = <<sp>>.largeurModuleBase
  expr: Constraints[14] = <<sp>>.insertFavDistAuZeroDuPLan
  expr: Constraints[15] = <<sp>>.epaisseurParois
  expr: Constraints[16] = <<sp>>.epaisseurParois
  sketch-geometry (6):
    g0: LineSegment StartX=-143.5 StartY=14.7426 StartZ=0 EndX=-147.5 EndY=14.7426 EndZ=0
    g1: LineSegment StartX=-147.5 StartY=14.7426 StartZ=0 EndX=-147.5 EndY=6.74264 EndZ=0
    g2: LineSegment StartX=-147.5 StartY=6.74264 StartZ=0 EndX=-139.5 EndY=6.74264 EndZ=0
    g3: LineSegment StartX=-139.5 StartY=6.74264 StartZ=0 EndX=-139.5 EndY=10.7426 EndZ=0
    g4: ArcOfCircle CenterX=-143.5 CenterY=10.7426 CenterZ=0 NormalX=0 NormalY=0 NormalZ=1 AngleXU=0 Radius=4 StartAngle=0 EndAngle=1.5708
    g5: GeomPoint X=-150 Y=4.24264 Z=0
  constraints (17):
    c: Horizontal(g0)
    c: Coincident(g0,g1)
    c: Vertical(g1)
    c: Coincident(g1,g2)
    c: Horizontal(g2)
    c: Coincident(g2,g3)
    c: Vertical(g3)
    c: Equal(g3,g0)
    c: Equal(g2,g1)
    c: Coincident(g0,g4)
    c: DistanceX(g2,g2) = 8
    c: Tangent(g4,g3) = -1.5708
    c: DistanceX(g0,g0) = 4
    c: DistanceX(g5,g-1) = 150
    c: DistanceY(g-1,g5) = 4.24264
    c: DistanceY(g5,g1) = 2.5
    c: DistanceX(g5,g1) = 2.5
FEATURE [PartDesign::Pad] Pad006  label="padInsertFavGauch"
  AllowMultiFace = false
  BaseFeature = -> Pad005
  Direction = (1,1,1)
  Length = 10
  Length2 = 100
  Profile = -> Sketch017
  Type = 2
FEATURE [Sketcher::SketchObject] Sketch018  label="skPercageInsertFavDroit"
  FullyConstrained = true
  MapMode = 5
  Placement = pos=(0,-71,-2.13e-14) rot=(1,0,0;0.785398rad)
  Support = -> [DatumPlane007]
  expr: Constraints[0] = <<sp>>.insertDiamPercage
  expr: Constraints[1] = <<sp>>.insertFavDistAuZeroDuPLan + <<sp>>.epaisseurParois + <<sp>>.insertFAVDistBord / 2
  expr: Constraints[2] = <<sp>>.epaisseurParois + <<sp>>.insertFAVDistBord / 2
  expr: Constraints[7] = <<sp>>.largeurModuleBase - 2 * <<sp>>.epaisseurParois - <<sp>>.insertFAVDistBord
  sketch-geometry (3):
    g0: Circle CenterX=-6.5 CenterY=10.7426 CenterZ=0 NormalX=0 NormalY=0 NormalZ=1 AngleXU=0 Radius=2
    g1: Circle CenterX=-143.5 CenterY=10.7426 CenterZ=0 NormalX=0 NormalY=0 NormalZ=1 AngleXU=0 Radius=2
    g2: LineSegment StartX=-143.5 StartY=10.7426 StartZ=0 EndX=-6.5 EndY=10.7426 EndZ=0
  constraints (8):
    c: Diameter(g0) = 4
    c: DistanceY(g-1,g0) = 10.7426
    c: DistanceX(g0,g-1) = 6.5
    c: Equal(g0,g1)
    c: Coincident(g2,g1)
    c: Coincident(g2,g0)
    c: Horizontal(g2)
    c: DistanceX(g2,g2) = 137
FEATURE [PartDesign::Pocket] Pocket010  label="trouInsertFavDroit"
  AllowMultiFace = false
  BaseFeature = -> Pad006
  Direction = (1,1,1)
  Length = 8
  Length2 = 100
  Profile = -> Sketch018
  Reversed = true
  Type = 0
  expr: Length = <<sp>>.insertFavProfondeur
FEATURE [PartDesign::Plane] DatumPlane011  label="planFaceAvant"
  AttachmentOffset = pos=(0,0,93.2843) rot=(-1,0,0;0.785398rad)
  Length = 206.452
  MapMode = 5
  Placement = pos=(0,-93.2843,-2.07e-14) rot=(1,0,0;0.785398rad)
  ResizeMode = 0
  Support = -> [XZ_Plane003]
  Width = 172.769
  expr: .AttachmentOffset.Base.z = <<sp>>.planFaceAvant
FEATURE [Sketcher::SketchObject] Sketch030  label="sk_rebordFav"
  FullyConstrained = true
  MapMode = 5
  Placement = pos=(0,-71,-2.13e-14) rot=(1,0,0;0.785398rad)
  Support = -> [DatumPlane007]
  expr: Constraints[0] = <<sp>>.insertFavDistAuZeroDuPLan
  expr: Constraints[19] = <<sp>>.epaisseurParois
  expr: Constraints[20] = <<sp>>.favEpBordure
  expr: Constraints[21] = <<sp>>.favDistBordPlan
  expr: Constraints[22] = <<sp>>.largeurModuleBase - 2 * <<sp>>.epaisseurParois
  expr: Constraints[23] = <<sp>>.favEpBordure
  expr: Constraints[24] = <<sp>>.Face - <<sp>>.epaisseurParois
  expr: Constraints[25] = <<sp>>.favEpBordure
  sketch-geometry (9):
    g0: GeomPoint X=0 Y=4.24264 Z=0
    g1: LineSegment StartX=-147.5 StartY=20.9853 StartZ=0 EndX=-147.5 EndY=81.7426 EndZ=0
    g2: LineSegment StartX=-147.5 StartY=81.7426 StartZ=0 EndX=-2.5 EndY=81.7426 EndZ=0
    g3: LineSegment StartX=-2.5 StartY=81.7426 StartZ=0 EndX=-2.5 EndY=20.9853 EndZ=0
    g4: LineSegment StartX=-2.5 StartY=20.9853 StartZ=0 EndX=-4 EndY=20.9853 EndZ=0
    g5: LineSegment StartX=-4 StartY=20.9853 StartZ=0 EndX=-4 EndY=80.2426 EndZ=0
    g6: LineSegment StartX=-4 StartY=80.2426 StartZ=0 EndX=-146 EndY=80.2426 EndZ=0
    g7: LineSegment StartX=-146 StartY=80.2426 StartZ=0 EndX=-146 EndY=20.9853 EndZ=0
    g8: LineSegment StartX=-146 StartY=20.9853 StartZ=0 EndX=-147.5 EndY=20.9853 EndZ=0
  constraints (26):
    c: DistanceY(g-1,g0) = 4.24264
    c: Vertical(g0,g-1)
    c: Vertical(g1)
    c: Coincident(g1,g2)
    c: Horizontal(g2)
    c: Coincident(g2,g3)
    c: Vertical(g3)
    c: Coincident(g3,g4)
    c: Horizontal(g4)
    c: Coincident(g4,g5)
    c: Vertical(g5)
    c: Coincident(g5,g6)
    c: Horizontal(g6)
    c: Coincident(g6,g7)
    c: Vertical(g7)
    c: Coincident(g7,g8)
    c: Coincident(g8,g1)
    c: Horizontal(g8)
    c: Horizontal(g7,g4)
    c: DistanceX(g3,g0) = 2.5
    c: DistanceX(g4,g4) = 1.5
    c: DistanceY(g0,g3) = 16.7426
    c: DistanceX(g1,g3) = 145
    c: DistanceY(g5,g2) = 1.5
    c: DistanceY(g0,g2) = 77.5
    c: DistanceX(g1,g7) = 1.5
FEATURE [PartDesign::Pad] Pad014  label="favRebordSupport"
  AllowMultiFace = false
  BaseFeature = -> Pocket010
  Direction = (1,1,1)
  Length = 10
  Length2 = 100
  Profile = -> Sketch030
  Type = 3
  UpToFace = -> Pocket010 [Face13]
FEATURE [PartDesign::Pad] Pad015  label="favRebord"
  AllowMultiFace = false
  BaseFeature = -> Pad014
  Direction = (1,1,1)
  Length = 4.15
  Length2 = 100
  Profile = -> Sketch030
  Reversed = true
  Type = 0
  expr: Length = <<sp>>.favBordureProf
FEATURE [Sketcher::SketchObject] Sketch031  label="sk_bourlet"
  ExternalGeometry = -> [Pad015]
  FullyConstrained = true
  MapMode = 5
  Placement = pos=(-2.5,0,0) rot=(0.57735,0.57735,0.57735;2.0944rad)
  Support = -> [Pad015]
  expr: Constraints[3] = <<sp>>.bourletMaintientRayon - <<sp>>.bourletRayonJeu
  sketch-geometry (2):
    g0: ArcOfCircle CenterX=-11.184 CenterY=55.7855 CenterZ=0 NormalX=0 NormalY=0 NormalZ=1 AngleXU=0 Radius=1.3 StartAngle=5.49779 EndAngle=8.63938
    g1: LineSegment StartX=-12.1032 StartY=56.7048 StartZ=0 EndX=-10.2647 EndY=54.8663 EndZ=0
  constraints (6):
    c: Coincident(g0,g-3)
    c: PointOnObject(g0,g-3)
    c: PointOnObject(g0,g-3)
    c: Radius(g0) = 1.3
    c: Coincident(g1,g0)
    c: Coincident(g1,g0)
FEATURE [PartDesign::Pad] Pad016  label="bourlet"
  AllowMultiFace = false
  BaseFeature = -> Pad015
  Direction = (1,1,1)
  Length = 10
  Length2 = 100
  Profile = -> Sketch031
  Reversed = true
  Type = 3
  UpToFace = -> Pad015 [Face11]
FEATURE [Sketcher::SketchObject] Sketch034  label="favTrous001"
  FullyConstrained = true
  MapMode = 5
  Placement = pos=(0,-93.2843,-2.84e-14) rot=(1,0,0;0.785398rad)
  Support = -> [DatumPlane011]
  expr: Constraints[10] = <<sp>>.distZeroPlanFAV
  expr: Constraints[12] = <<favTrous>>.switchPosX
  expr: Constraints[13] = <<favTrous>>.switchPosY
  expr: Constraints[27] = <<favTrous>>.oscilloDistTrousX
  expr: Constraints[28] = <<favTrous>>.oscilloTrouDiam
  expr: Constraints[29] = <<favTrous>>.oscilloDistTrousY
  expr: Constraints[30] = <<favTrous>>.oscilloTrou1PosX
  expr: Constraints[31] = <<favTrous>>.oscilloTrou1PosY
  expr: Constraints[8] = <<SW_C1500AT>>.trouLargeur
  expr: Constraints[9] = <<SW_C1500AT>>.trouLongeur
  sketch-geometry (12):
    g0: LineSegment StartX=-142.55 StartY=88.25 StartZ=0 EndX=-131 EndY=88.25 EndZ=0
    g1: LineSegment StartX=-131 StartY=88.25 StartZ=0 EndX=-131 EndY=60 EndZ=0
    g2: LineSegment StartX=-131 StartY=60 StartZ=0 EndX=-142.55 EndY=60 EndZ=0
    g3: LineSegment StartX=-142.55 StartY=60 StartZ=0 EndX=-142.55 EndY=88.25 EndZ=0
    g4: GeomPoint X=0 Y=20 Z=0
    g5: Circle CenterX=-15 CenterY=27 CenterZ=0 NormalX=0 NormalY=0 NormalZ=1 AngleXU=0 Radius=2
    g6: Circle CenterX=-122 CenterY=27 CenterZ=0 NormalX=0 NormalY=0 NormalZ=1 AngleXU=0 Radius=2
    g7: Circle CenterX=-122 CenterY=93 CenterZ=0 NormalX=0 NormalY=0 NormalZ=1 AngleXU=0 Radius=2
    g8: Circle CenterX=-15 CenterY=93 CenterZ=0 NormalX=0 NormalY=0 NormalZ=1 AngleXU=0 Radius=2
    g9: LineSegment StartX=-122 StartY=93 StartZ=0 EndX=-15 EndY=93 EndZ=0
    g10: LineSegment StartX=-15 StartY=93 StartZ=0 EndX=-15 EndY=27 EndZ=0
    g11: LineSegment StartX=-15 StartY=27 StartZ=0 EndX=-122 EndY=27 EndZ=0
  constraints (32):
    c: Coincident(g0,g1)
    c: Coincident(g1,g2)
    c: Coincident(g2,g3)
    c: Coincident(g3,g0)
    c: Horizontal(g0)
    c: Horizontal(g2)
    c: Vertical(g1)
    c: Vertical(g3)
    c: DistanceX(g0,g0) = 11.55
    c: DistanceY(g1,g1) = 28.25
    c: DistanceY(g-1,g4) = 20
    c: Vertical(g4,g-1)
    c: DistanceX(g1,g4) = 131
    c: DistanceY(g4,g1) = 40
    c: Equal(g8,g7)
    c: Equal(g8,g5)
    c: Equal(g6,g5)
    c: Coincident(g9,g7)
    c: Coincident(g9,g8)
    c: Horizontal(g9)
    c: Coincident(g10,g8)
    c: Coincident(g10,g5)
    c: Vertical(g10)
    c: Coincident(g11,g5)
    c: Coincident(g11,g6)
    c: Horizontal(g11)
    c: Equal(g9,g11)
    c: DistanceX(g9,g9) = 107
    c: Diameter(g8) = 4
    c: DistanceY(g10,g10) = 66
    c: DistanceX(g5,g4) = 15
    c: DistanceY(g4,g5) = 7
FEATURE [PartDesign::Pocket] Pocket016  label="trousFav"
  BaseFeature = -> Pad016
  Direction = (1,1,1)
  Length = 5
  Length2 = 100
  Profile = -> Sketch034
  Type = 1
FEATURE [Sketcher::SketchObject] Sketch035  label="sk_trousAlimSignal"
  FullyConstrained = true
  MapMode = 5
  Placement = pos=(0,-93.2843,-2.84e-14) rot=(1,0,0;0.785398rad)
  Support = -> [DatumPlane011]
  expr: Constraints[0] = <<sp>>.distZeroPlanFAV
  expr: Constraints[2] = <<favTrous>>.oscilloTrouAlimPosX
  expr: Constraints[3] = <<favTrous>>.oscilloTrouAlimPosY
  expr: Constraints[4] = <<favTrous>>.oscilloTrouAlimDiam
  expr: Constraints[5] = <<favTrous>>.bncDiam
  expr: Constraints[6] = <<favTrous>>.signalTrouPosX
  expr: Constraints[7] = <<favTrous>>.signalTrouPosY
  sketch-geometry (3):
    g0: Circle CenterX=-31 CenterY=90 CenterZ=0 NormalX=0 NormalY=0 NormalZ=1 AngleXU=0 Radius=3.5
    g1: GeomPoint X=0 Y=20 Z=0
    g2: Circle CenterX=-111 CenterY=87 CenterZ=0 NormalX=0 NormalY=0 NormalZ=1 AngleXU=0 Radius=5.15
  constraints (8):
    c: DistanceY(g-1,g1) = 20
    c: Vertical(g1,g-1)
    c: DistanceX(g0,g1) = 31
    c: DistanceY(g1,g0) = 70
    c: Diameter(g0) = 7
    c: Diameter(g2) = 10.3
    c: DistanceX(g2,g1) = 111
    c: DistanceY(g1,g2) = 67
FEATURE [PartDesign::Pocket] Pocket017  label="trouSignalEtAlim"
  BaseFeature = -> Pocket016
  Direction = (1,1,1)
  Length = 5
  Length2 = 100
  Profile = -> Sketch035
  Type = 1
FEATURE [Sketcher::SketchObject] Sketch036  label="sk_favTrouBnc"
  FullyConstrained = true
  MapMode = 5
  Placement = pos=(0,-93.2843,-2.84e-14) rot=(1,0,0;0.785398rad)
  Support = -> [DatumPlane011]
  expr: Constraints[0] = <<sp>>.distZeroPlanFAV
  expr: Constraints[2] = <<favTrous>>.bncPosX
  expr: Constraints[3] = <<favTrous>>.bncPosY
  expr: Constraints[4] = <<favTrous>>.bncDiam
  expr: Constraints[8] = <<bnc>>.trouMeplatDepuisLeCentre + <<bnc>>.trouJeu
  sketch-geometry (3):
    g0: ArcOfCircle CenterX=-137 CenterY=42 CenterZ=0 NormalX=0 NormalY=0 NormalZ=1 AngleXU=0 Radius=5.15 StartAngle=0.696659 EndAngle=5.58653
    g1: GeomPoint X=0 Y=20 Z=0
    g2: LineSegment StartX=-133.05 StartY=45.3045 StartZ=0 EndX=-133.05 EndY=38.6955 EndZ=0
  constraints (9):
    c: DistanceY(g-1,g1) = 20
    c: Vertical(g1,g-1)
    c: DistanceX(g0,g1) = 137
    c: DistanceY(g1,g0) = 22
    c: Diameter(g0) = 10.3
    c: Vertical(g2)
    c: Coincident(g0,g2)
    c: Coincident(g0,g2)
    c: DistanceX(g0,g0) = 3.95
FEATURE [PartDesign::Pocket] Pocket018  label="trouBNC"
  BaseFeature = -> Pocket017
  Direction = (1,1,1)
  Length = 5
  Length2 = 100
  Profile = -> Sketch036
  Type = 1
FEATURE [PartDesign::Body] Body002  label="faceAvant"
  BaseFeature = -> Slice_child1
  Group = -> [Clone001,Thickness001,DatumPlane007,Sketch016,Pad005,Sketch017,Pad006,Sketch018,Pocket010,DatumPlane011,Sketch030,Pad014,Pad015,Sketch031,Pad016,Sketch034,Pocket016,Sketch035,Pocket017,Sketch036,Pocket018]
  Origin = -> Origin003
  Tip = -> Pocket018
COMPONENT P2 — recipe-attached ("visTHCM3x10_001", modeled in this document).
Construction recipe (the document's own serialized feature program — sketch geometry with constraints, then the solid features built on it; lengths are millimeters unless a unit is written):

FEATURE [Sketcher::SketchObject] Sketch020
  FullyConstrained = false
  MapMode = 5
  Support = -> [XY_Plane006]
  sketch-geometry (1):
    g0: Circle CenterX=0 CenterY=0 CenterZ=0 NormalX=0 NormalY=0 NormalZ=1 AngleXU=0 Radius=2.75
  constraints (2):
    c: Coincident(g0,g-1)
    c: Diameter(g0) = 5.5
FEATURE [PartDesign::Pad] Pad008  label="tete"
  AllowMultiFace = false
  Direction = (1,1,1)
  Length = 3
  Length2 = 100
  Profile = -> Sketch020
  Type = 0
FEATURE [Sketcher::SketchObject] Sketch001
  FullyConstrained = false
  MapMode = 5
  Placement = pos=(0,0,0) rot=(1,0,0;3.14159rad)
  Support = -> [Pad008]
  sketch-geometry (1):
    g0: Circle CenterX=0 CenterY=0 CenterZ=0 NormalX=0 NormalY=0 NormalZ=1 AngleXU=0 Radius=1.5
  constraints (2):
    c: Coincident(g0,g-1)
    c: Diameter(g0) = 3
FEATURE [PartDesign::Pad] Pad009  label="corps"
  AllowMultiFace = false
  BaseFeature = -> Pad008
  Direction = (1,1,1)
  Length = 10
  Length2 = 100
  Profile = -> Sketch001
  Type = 0
FEATURE [PartDesign::Plane] DatumPlane008
  AttachmentOffset = pos=(0,0,3) rot=(0,0,1;0rad)
  Length = 60
  MapMode = 5
  Placement = pos=(0,0,3) rot=(0,0,1;0rad)
  ResizeMode = 0
  Support = -> [XY_Plane006]
  Width = 60
FEATURE [Sketcher::SketchObject] Sketch021
  FullyConstrained = false
  MapMode = 5
  Placement = pos=(0,0,3) rot=(0,0,1;0rad)
  Support = -> [DatumPlane008]
  sketch-geometry (7):
    g0: LineSegment StartX=0.721688 StartY=-1.25 StartZ=0 EndX=1.44338 EndY=1.0119e-12 EndZ=0
    g1: LineSegment StartX=1.44338 StartY=1.0119e-12 StartZ=0 EndX=0.721688 EndY=1.25 EndZ=0
    g2: LineSegment StartX=0.721688 StartY=1.25 StartZ=0 EndX=-0.721688 EndY=1.25 EndZ=0
    g3: LineSegment StartX=-0.721688 StartY=1.25 StartZ=0 EndX=-1.44338 EndY=8.689e-13 EndZ=0
    g4: LineSegment StartX=-1.44338 StartY=8.689e-13 StartZ=0 EndX=-0.721688 EndY=-1.25 EndZ=0
    g5: LineSegment StartX=-0.721688 StartY=-1.25 StartZ=0 EndX=0.721688 EndY=-1.25 EndZ=0
    g6: Circle CenterX=0 CenterY=0 CenterZ=0 NormalX=0 NormalY=0 NormalZ=1 AngleXU=0 Radius=1.44338
  constraints (16):
    c: Coincident(g0,g1)
    c: Coincident(g1,g2)
    c: Coincident(g2,g3)
    c: Coincident(g3,g4)
    c: Coincident(g4,g5)
    c: Coincident(g5,g0)
    c: Equal(g0, g1-g5) x5
    c: PointOnObject(g0,g6)
    c: PointOnObject(g1,g6)
    c: PointOnObject(g2,g6)
    c: PointOnObject(g3,g6)
    c: PointOnObject(g4,g6)
    c: PointOnObject(g5,g6)
    c: Coincident(g6,g-1)
    c: Horizontal(g2)
    c: DistanceY(g0,g1) = 2.5
FEATURE [PartDesign::Pocket] Pocket011  label="emprunte"
  AllowMultiFace = false
  BaseFeature = -> Pad009
  Direction = (1,1,1)
  Length = 4
  Length2 = 100
  Profile = -> Sketch021
  Type = 0
FEATURE [PartDesign::Body] Body003  label="visTHCM3x10_001"
  Group = -> [Sketch020,Pad008,Sketch001,Pad009,DatumPlane008,Sketch021,Pocket011]
  Origin = -> Origin010
  Placement = pos=(-6.5,-61.582,5.72756) rot=(1,0,0;3.92699rad)
  Tip = -> Pocket011
COMPONENT P3 — recipe-attached ("visTHCM3x10_002", modeled in this document).
Construction recipe (the document's own serialized feature program — sketch geometry with constraints, then the solid features built on it; lengths are millimeters unless a unit is written):

FEATURE [PartDesign::Plane] DatumPlane009
  AttachmentOffset = pos=(0,0,3) rot=(0,0,1;0rad)
  Length = 60
  MapMode = 5
  Placement = pos=(0,0,3) rot=(0,0,1;0rad)
  ResizeMode = 0
  Support = -> [XY_Plane007]
  Width = 60
FEATURE [Sketcher::SketchObject] Sketch022
  FullyConstrained = false
  MapMode = 5
  Support = -> [XY_Plane007]
  sketch-geometry (1):
    g0: Circle CenterX=0 CenterY=0 CenterZ=0 NormalX=0 NormalY=0 NormalZ=1 AngleXU=0 Radius=2.75
  constraints (2):
    c: Coincident(g0,g-1)
    c: Diameter(g0) = 5.5
FEATURE [PartDesign::Pad] Pad011  label="tete001"
  AllowMultiFace = false
  Direction = (1,1,1)
  Length = 3
  Length2 = 100
  Profile = -> Sketch022
  Type = 0
FEATURE [Sketcher::SketchObject] Sketch023
  FullyConstrained = false
  MapMode = 5
  Placement = pos=(0,0,0) rot=(1,0,0;3.14159rad)
  Support = -> [Pad011]
  sketch-geometry (1):
    g0: Circle CenterX=0 CenterY=0 CenterZ=0 NormalX=0 NormalY=0 NormalZ=1 AngleXU=0 Radius=1.5
  constraints (2):
    c: Coincident(g0,g-1)
    c: Diameter(g0) = 3
FEATURE [PartDesign::Pad] Pad010  label="corps001"
  AllowMultiFace = false
  BaseFeature = -> Pad011
  Direction = (1,1,1)
  Length = 10
  Length2 = 100
  Profile = -> Sketch023
  Type = 0
FEATURE [Sketcher::SketchObject] Sketch024
  FullyConstrained = false
  MapMode = 5
  Placement = pos=(0,0,3) rot=(0,0,1;0rad)
  Support = -> [DatumPlane009]
  sketch-geometry (7):
    g0: LineSegment StartX=0.721688 StartY=-1.25 StartZ=0 EndX=1.44338 EndY=1.0119e-12 EndZ=0
    g1: LineSegment StartX=1.44338 StartY=1.0119e-12 StartZ=0 EndX=0.721688 EndY=1.25 EndZ=0
    g2: LineSegment StartX=0.721688 StartY=1.25 StartZ=0 EndX=-0.721688 EndY=1.25 EndZ=0
    g3: LineSegment StartX=-0.721688 StartY=1.25 StartZ=0 EndX=-1.44338 EndY=8.689e-13 EndZ=0
    g4: LineSegment StartX=-1.44338 StartY=8.689e-13 StartZ=0 EndX=-0.721688 EndY=-1.25 EndZ=0
    g5: LineSegment StartX=-0.721688 StartY=-1.25 StartZ=0 EndX=0.721688 EndY=-1.25 EndZ=0
    g6: Circle CenterX=0 CenterY=0 CenterZ=0 NormalX=0 NormalY=0 NormalZ=1 AngleXU=0 Radius=1.44338
  constraints (16):
    c: Coincident(g0,g1)
    c: Coincident(g1,g2)
    c: Coincident(g2,g3)
    c: Coincident(g3,g4)
    c: Coincident(g4,g5)
    c: Coincident(g5,g0)
    c: Equal(g0, g1-g5) x5
    c: PointOnObject(g0,g6)
    c: PointOnObject(g1,g6)
    c: PointOnObject(g2,g6)
    c: PointOnObject(g3,g6)
    c: PointOnObject(g4,g6)
    c: PointOnObject(g5,g6)
    c: Coincident(g6,g-1)
    c: Horizontal(g2)
    c: DistanceY(g0,g1) = 2.5
FEATURE [PartDesign::Pocket] Pocket012  label="emprunte001"
  AllowMultiFace = false
  BaseFeature = -> Pad010
  Direction = (1,1,1)
  Length = 4
  Length2 = 100
  Profile = -> Sketch024
  Type = 0
FEATURE [PartDesign::Body] Body004  label="visTHCM3x10_002"
  Group = -> [Sketch022,Pad011,Sketch023,Pad010,DatumPlane009,Sketch024,Pocket012]
  Origin = -> Origin011
  Placement = pos=(-143.5,-61.582,5.72756) rot=(1,0,0;3.92699rad)
  Tip = -> Pocket012
COMPONENT P4 — recipe-attached ("visTHCM3x6_FAV001", modeled in this document).
Construction recipe (the document's own serialized feature program — sketch geometry with constraints, then the solid features built on it; lengths are millimeters unless a unit is written):

FEATURE [Sketcher::SketchObject] Sketch047
  FullyConstrained = false
  MapMode = 5
  Support = -> [XY_Plane046]
  sketch-geometry (1):
    g0: Circle CenterX=0 CenterY=0 CenterZ=0 NormalX=0 NormalY=0 NormalZ=1 AngleXU=0 Radius=2.75
  constraints (2):
    c: Coincident(g0,g-1)
    c: Diameter(g0) = 5.5
FEATURE [PartDesign::Pad] Pad024  label="tete004"
  AllowMultiFace = false
  Direction = (1,1,1)
  Length = 3
  Length2 = 100
  Profile = -> Sketch047
  Type = 0
FEATURE [Sketcher::SketchObject] Sketch048
  FullyConstrained = false
  MapMode = 5
  Placement = pos=(0,0,0) rot=(1,0,0;3.14159rad)
  Support = -> [Pad024]
  sketch-geometry (1):
    g0: Circle CenterX=0 CenterY=0 CenterZ=0 NormalX=0 NormalY=0 NormalZ=1 AngleXU=0 Radius=1.5
  constraints (2):
    c: Coincident(g0,g-1)
    c: Diameter(g0) = 3
FEATURE [PartDesign::Pad] Pad025  label="corps004"
  AllowMultiFace = false
  BaseFeature = -> Pad024
  Direction = (1,1,1)
  Length = 6
  Length2 = 100
  Profile = -> Sketch048
  Type = 0
FEATURE [PartDesign::Plane] DatumPlane018
  AttachmentOffset = pos=(0,0,3) rot=(0,0,1;0rad)
  Length = 60
  MapMode = 5
  Placement = pos=(0,0,3) rot=(0,0,1;0rad)
  ResizeMode = 0
  Support = -> [XY_Plane046]
  Width = 60
FEATURE [Sketcher::SketchObject] Sketch049
  FullyConstrained = false
  MapMode = 5
  Placement = pos=(0,0,3) rot=(0,0,1;0rad)
  Support = -> [DatumPlane018]
  sketch-geometry (7):
    g0: LineSegment StartX=0.721688 StartY=-1.25 StartZ=0 EndX=1.44338 EndY=1.0119e-12 EndZ=0
    g1: LineSegment StartX=1.44338 StartY=1.0119e-12 StartZ=0 EndX=0.721688 EndY=1.25 EndZ=0
    g2: LineSegment StartX=0.721688 StartY=1.25 StartZ=0 EndX=-0.721688 EndY=1.25 EndZ=0
    g3: LineSegment StartX=-0.721688 StartY=1.25 StartZ=0 EndX=-1.44338 EndY=8.689e-13 EndZ=0
    g4: LineSegment StartX=-1.44338 StartY=8.689e-13 StartZ=0 EndX=-0.721688 EndY=-1.25 EndZ=0
    g5: LineSegment StartX=-0.721688 StartY=-1.25 StartZ=0 EndX=0.721688 EndY=-1.25 EndZ=0
    g6: Circle CenterX=0 CenterY=0 CenterZ=0 NormalX=0 NormalY=0 NormalZ=1 AngleXU=0 Radius=1.44338
  constraints (16):
    c: Coincident(g0,g1)
    c: Coincident(g1,g2)
    c: Coincident(g2,g3)
    c: Coincident(g3,g4)
    c: Coincident(g4,g5)
    c: Coincident(g5,g0)
    c: Equal(g0, g1-g5) x5
    c: PointOnObject(g0,g6)
    c: PointOnObject(g1,g6)
    c: PointOnObject(g2,g6)
    c: PointOnObject(g3,g6)
    c: PointOnObject(g4,g6)
    c: PointOnObject(g5,g6)
    c: Coincident(g6,g-1)
    c: Horizontal(g2)
    c: DistanceY(g0,g1) = 2.5
FEATURE [PartDesign::Pocket] Pocket022  label="emprunte004"
  AllowMultiFace = false
  BaseFeature = -> Pad025
  Direction = (1,1,1)
  Length = 4
  Length2 = 100
  Profile = -> Sketch049
  Type = 0
FEATURE [PartDesign::Body] Body013  label="visTHCM3x6_FAV001"
  Group = -> [Sketch047,Pad024,Sketch048,Pad025,DatumPlane018,Sketch049,Pocket022]
  Origin = -> Origin048
  Placement = pos=(-6.46,-61.9464,6.08988) rot=(1,0,0;3.92699rad)
  Tip = -> Pocket022
COMPONENT P5 — recipe-attached ("visTHCM3x6_FAV002", modeled in this document).
Construction recipe (the document's own serialized feature program — sketch geometry with constraints, then the solid features built on it; lengths are millimeters unless a unit is written):

FEATURE [PartDesign::Plane] DatumPlane019
  AttachmentOffset = pos=(0,0,3) rot=(0,0,1;0rad)
  Length = 60
  MapMode = 5
  Placement = pos=(0,0,3) rot=(0,0,1;0rad)
  ResizeMode = 0
  Support = -> [XY_Plane047]
  Width = 60
FEATURE [Sketcher::SketchObject] Sketch051
  FullyConstrained = false
  MapMode = 5
  Support = -> [XY_Plane047]
  sketch-geometry (1):
    g0: Circle CenterX=0 CenterY=0 CenterZ=0 NormalX=0 NormalY=0 NormalZ=1 AngleXU=0 Radius=2.75
  constraints (2):
    c: Coincident(g0,g-1)
    c: Diameter(g0) = 5.5
FEATURE [PartDesign::Pad] Pad027  label="tete005"
  AllowMultiFace = false
  Direction = (1,1,1)
  Length = 3
  Length2 = 100
  Profile = -> Sketch051
  Type = 0
FEATURE [Sketcher::SketchObject] Sketch050
  FullyConstrained = false
  MapMode = 5
  Placement = pos=(0,0,0) rot=(1,0,0;3.14159rad)
  Support = -> [Pad027]
  sketch-geometry (1):
    g0: Circle CenterX=0 CenterY=0 CenterZ=0 NormalX=0 NormalY=0 NormalZ=1 AngleXU=0 Radius=1.5
  constraints (2):
    c: Coincident(g0,g-1)
    c: Diameter(g0) = 3
FEATURE [PartDesign::Pad] Pad026  label="corps005"
  AllowMultiFace = false
  BaseFeature = -> Pad027
  Direction = (1,1,1)
  Length = 6
  Length2 = 100
  Profile = -> Sketch050
  Type = 0
FEATURE [Sketcher::SketchObject] Sketch052
  FullyConstrained = false
  MapMode = 5
  Placement = pos=(0,0,3) rot=(0,0,1;0rad)
  Support = -> [DatumPlane019]
  sketch-geometry (7):
    g0: LineSegment StartX=0.721688 StartY=-1.25 StartZ=0 EndX=1.44338 EndY=1.0119e-12 EndZ=0
    g1: LineSegment StartX=1.44338 StartY=1.0119e-12 StartZ=0 EndX=0.721688 EndY=1.25 EndZ=0
    g2: LineSegment StartX=0.721688 StartY=1.25 StartZ=0 EndX=-0.721688 EndY=1.25 EndZ=0
    g3: LineSegment StartX=-0.721688 StartY=1.25 StartZ=0 EndX=-1.44338 EndY=8.689e-13 EndZ=0
    g4: LineSegment StartX=-1.44338 StartY=8.689e-13 StartZ=0 EndX=-0.721688 EndY=-1.25 EndZ=0
    g5: LineSegment StartX=-0.721688 StartY=-1.25 StartZ=0 EndX=0.721688 EndY=-1.25 EndZ=0
    g6: Circle CenterX=0 CenterY=0 CenterZ=0 NormalX=0 NormalY=0 NormalZ=1 AngleXU=0 Radius=1.44338
  constraints (16):
    c: Coincident(g0,g1)
    c: Coincident(g1,g2)
    c: Coincident(g2,g3)
    c: Coincident(g3,g4)
    c: Coincident(g4,g5)
    c: Coincident(g5,g0)
    c: Equal(g0, g1-g5) x5
    c: PointOnObject(g0,g6)
    c: PointOnObject(g1,g6)
    c: PointOnObject(g2,g6)
    c: PointOnObject(g3,g6)
    c: PointOnObject(g4,g6)
    c: PointOnObject(g5,g6)
    c: Coincident(g6,g-1)
    c: Horizontal(g2)
    c: DistanceY(g0,g1) = 2.5
FEATURE [PartDesign::Pocket] Pocket023  label="emprunte005"
  AllowMultiFace = false
  BaseFeature = -> Pad026
  Direction = (1,1,1)
  Length = 4
  Length2 = 100
  Profile = -> Sketch052
  Type = 0
FEATURE [PartDesign::Body] Body014  label="visTHCM3x6_FAV002"
  Group = -> [Sketch051,Pad027,Sketch050,Pad026,DatumPlane019,Sketch052,Pocket023]
  Origin = -> Origin049
  Placement = pos=(-143.48,-61.9464,6.08988) rot=(1,0,0;3.92699rad)
  Tip = -> Pocket023
COMPONENT P6 — recipe-attached ("Part", modeled in this document).
Construction recipe (the document's own serialized feature program — sketch geometry with constraints, then the solid features built on it; lengths are millimeters unless a unit is written):

FEATURE [Sketcher::SketchObject] Sketch  label="profileDeBase"
  FullyConstrained = true
  MapMode = 5
  Placement = pos=(0,0,0) rot=(0.57735,0.57735,0.57735;2.0944rad)
  Support = -> [YZ_Plane001]
  expr: Constraints[10] = <<sp>>.petitRetour
  expr: Constraints[11] = <<sp>>.angleFacePetitRetour
  expr: Constraints[12] = <<sp>>.Face
  expr: Constraints[13] = <<sp>>.angleFaceRetourHaut
  expr: Constraints[8] = <<sp>>.Base
  expr: Constraints[9] = <<sp>>.anglePetitRetourBase
  sketch-geometry (5):
    g0: LineSegment StartX=0 StartY=0 StartZ=0 EndX=-65 EndY=0 EndZ=0
    g1: LineSegment StartX=-65 StartY=0 StartZ=0 EndX=-79.1421 EndY=14.1421 EndZ=0
    g2: LineSegment StartX=-79.1421 StartY=14.1421 StartZ=0 EndX=-22.5736 EndY=70.7107 EndZ=0
    g3: LineSegment StartX=-22.5736 StartY=70.7107 StartZ=0 EndX=0 EndY=48.1371 EndZ=0
    g4: LineSegment StartX=0 StartY=48.1371 StartZ=0 EndX=0 EndY=0 EndZ=0
  constraints (14):
    c: Coincident(g-1,g0)
    c: Horizontal(g0)
    c: Coincident(g0,g1)
    c: Coincident(g1,g2)
    c: Coincident(g2,g3)
    c: PointOnObject(g3,g-2)
    c: Coincident(g3,g4)
    c: Coincident(g4,g0)
    c: DistanceX(g0,g0) = 65
    c: Angle(g0,g1) = 2.35619
    c: Distance(g1) = 20
    c: Angle(g1,g2) = 1.5708
    c: Distance(g2) = 80
    c: Angle(g2,g3) = 1.5708
FEATURE [PartDesign::Pad] Pad
  AllowMultiFace = false
  Direction = (1,1,1)
  Length = 150
  Length2 = 100
  Placement = pos=(0,0,0) rot=(0.57735,0.57735,0.57735;2.0944rad)
  Profile = -> Sketch
  Reversed = true
  Type = 0
  expr: Length = <<sp>>.largeurModuleBase
FEATURE [PartDesign::Plane] DatumPlane
  AttachmentOffset = pos=(71,0,0) rot=(0,-1,0;0.785398rad)
  Length = 98.6412
  MapMode = 5
  Placement = pos=(-7.9e-15,8e-15,71) rot=(0.678598,0.678598,0.281085;3.68962rad)
  ResizeMode = 0
  Support = -> [Pad]
  Width = 63.0813
FEATURE [PartDesign::Body] Body  label="Base"
  Group = -> [Sketch,Pad,DatumPlane]
  Origin = -> Origin001
  Tip = -> Pad
COMPONENT P7 — geometry summary ("xt60fem"; no construction recipe available for this part):
  bounding box: 20.5 x 16.5 x 7.5 mm
  tessellated surface: 20,392 triangles
  volume: 955 mm^3 (38% of its bounding box)
COMPONENT P8 — geometry summary ("xt60Male"; no construction recipe available for this part):
  bounding box: 20.2 x 16.6 x 7.5 mm
  tessellated surface: 13,748 triangles
  volume: 1201 mm^3 (48% of its bounding box)
COMPONENT P9 — geometry summary ("ZSB_RUTHEX_M3_5.7_001"; no construction recipe available for this part):
  bounding box: 5.7 x 4.6 x 4.6 mm
  tessellated surface: 4,632 triangles
  volume: 44 mm^3 (36% of its bounding box)
  symmetry: 4-fold rotationally symmetric about the y axis; mirror-symmetric across its x mid-plane, z mid-plane
COMPONENT P10 — geometry summary ("ZSB_RUTHEX_M3_5.7_002"; no construction recipe available for this part):
  bounding box: 5.7 x 4.6 x 4.6 mm
  tessellated surface: 4,632 triangles
  volume: 44 mm^3 (36% of its bounding box)
  symmetry: 4-fold rotationally symmetric about the y axis; mirror-symmetric across its x mid-plane, z mid-plane
COMPONENT P11 — geometry summary ("ZSB_RUTHEX_M3_5.7_003"; no construction recipe available for this part):
  bounding box: 6.9 x 6.9 x 4.6 mm
  tessellated surface: 4,632 triangles
  volume: 44 mm^3 (20% of its bounding box)
  symmetry: mirror-symmetric across its x mid-plane
COMPONENT P12 — geometry summary ("ZSB_RUTHEX_M3_5.7_004"; no construction recipe available for this part):
  bounding box: 6.9 x 6.9 x 4.6 mm
  tessellated surface: 4,632 triangles
  volume: 44 mm^3 (20% of its bounding box)
  symmetry: mirror-symmetric across its x mid-plane
COMPONENT P13 — recipe-attached ("partVisPointeauM3x10_001", modeled in this document).
Construction recipe (the document's own serialized feature program — sketch geometry with constraints, then the solid features built on it; lengths are millimeters unless a unit is written):

FEATURE [Sketcher::SketchObject] Sketch025
  FullyConstrained = false
  MapMode = 5
  Support = -> [XY_Plane008]
  sketch-geometry (1):
    g0: Circle CenterX=0 CenterY=0 CenterZ=0 NormalX=0 NormalY=0 NormalZ=1 AngleXU=0 Radius=1.5
  constraints (2):
    c: Coincident(g0,g-1)
    c: Diameter(g0) = 3
FEATURE [Sketcher::SketchObject] Sketch026
  FullyConstrained = false
  MapMode = 5
  Support = -> [XY_Plane008]
  sketch-geometry (7):
    g0: LineSegment StartX=0.433013 StartY=-0.75 StartZ=0 EndX=0.866025 EndY=1.25568e-11 EndZ=0
    g1: LineSegment StartX=0.866025 StartY=1.25568e-11 StartZ=0 EndX=0.433013 EndY=0.75 EndZ=0
    g2: LineSegment StartX=0.433013 StartY=0.75 StartZ=0 EndX=-0.433013 EndY=0.75 EndZ=0
    g3: LineSegment StartX=-0.433013 StartY=0.75 StartZ=0 EndX=-0.866025 EndY=2.91366e-11 EndZ=0
    g4: LineSegment StartX=-0.866025 StartY=2.91366e-11 StartZ=0 EndX=-0.433013 EndY=-0.75 EndZ=0
    g5: LineSegment StartX=-0.433013 StartY=-0.75 StartZ=0 EndX=0.433013 EndY=-0.75 EndZ=0
    g6: Circle CenterX=0 CenterY=0 CenterZ=0 NormalX=0 NormalY=0 NormalZ=1 AngleXU=0 Radius=0.866025
  constraints (16):
    c: Coincident(g0,g1)
    c: Coincident(g1,g2)
    c: Coincident(g2,g3)
    c: Coincident(g3,g4)
    c: Coincident(g4,g5)
    c: Coincident(g5,g0)
    c: Equal(g0, g1-g5) x5
    c: PointOnObject(g0,g6)
    c: PointOnObject(g1,g6)
    c: PointOnObject(g2,g6)
    c: PointOnObject(g3,g6)
    c: PointOnObject(g4,g6)
    c: PointOnObject(g5,g6)
    c: Coincident(g6,g-1)
    c: Horizontal(g2)
    c: DistanceY(g0,g1) = 1.5
FEATURE [PartDesign::Pad] Pad012
  AllowMultiFace = false
  Direction = (1,1,1)
  Length = 10
  Length2 = 100
  Profile = -> Sketch025
  Type = 0
FEATURE [PartDesign::Chamfer] Chamfer
  Angle = 45
  Base = -> Pad012 [Edge3]
  BaseFeature = -> Pad012
  ChamferType = 0
  FlipDirection = false
  Size = 1.4
  Size2 = 1
  SupportTransform = false
  UseAllEdges = false
FEATURE [PartDesign::Pocket] Pocket013
  AllowMultiFace = false
  BaseFeature = -> Chamfer
  Direction = (1,1,1)
  Length = 1.5
  Length2 = 100
  Profile = -> Sketch026
  Reversed = true
  Type = 0
FEATURE [PartDesign::Chamfer] Chamfer001
  Angle = 45
  Base = -> Pocket013 [Edge3]
  BaseFeature = -> Pocket013
  ChamferType = 0
  FlipDirection = false
  Size = 0.1
  Size2 = 1
  SupportTransform = false
  UseAllEdges = false
FEATURE [PartDesign::Body] Body005  label="bodyVisPointeauM3x10_001"
  Group = -> [Sketch025,Pad012,Chamfer,Sketch026,Pocket013,Chamfer001]
  Origin = -> Origin013
  Tip = -> Chamfer001
COMPONENT P14 — recipe-attached ("partVisPointeauM3x10_002", modeled in this document).
Construction recipe (the document's own serialized feature program — sketch geometry with constraints, then the solid features built on it; lengths are millimeters unless a unit is written):

FEATURE [Sketcher::SketchObject] Sketch027
  FullyConstrained = false
  MapMode = 5
  Support = -> [XY_Plane010]
  sketch-geometry (7):
    g0: LineSegment StartX=0.433013 StartY=-0.75 StartZ=0 EndX=0.866025 EndY=1.25568e-11 EndZ=0
    g1: LineSegment StartX=0.866025 StartY=1.25568e-11 StartZ=0 EndX=0.433013 EndY=0.75 EndZ=0
    g2: LineSegment StartX=0.433013 StartY=0.75 StartZ=0 EndX=-0.433013 EndY=0.75 EndZ=0
    g3: LineSegment StartX=-0.433013 StartY=0.75 StartZ=0 EndX=-0.866025 EndY=2.91366e-11 EndZ=0
    g4: LineSegment StartX=-0.866025 StartY=2.91366e-11 StartZ=0 EndX=-0.433013 EndY=-0.75 EndZ=0
    g5: LineSegment StartX=-0.433013 StartY=-0.75 StartZ=0 EndX=0.433013 EndY=-0.75 EndZ=0
    g6: Circle CenterX=0 CenterY=0 CenterZ=0 NormalX=0 NormalY=0 NormalZ=1 AngleXU=0 Radius=0.866025
  constraints (16):
    c: Coincident(g0,g1)
    c: Coincident(g1,g2)
    c: Coincident(g2,g3)
    c: Coincident(g3,g4)
    c: Coincident(g4,g5)
    c: Coincident(g5,g0)
    c: Equal(g0, g1-g5) x5
    c: PointOnObject(g0,g6)
    c: PointOnObject(g1,g6)
    c: PointOnObject(g2,g6)
    c: PointOnObject(g3,g6)
    c: PointOnObject(g4,g6)
    c: PointOnObject(g5,g6)
    c: Coincident(g6,g-1)
    c: Horizontal(g2)
    c: DistanceY(g0,g1) = 1.5
FEATURE [Sketcher::SketchObject] Sketch028
  FullyConstrained = false
  MapMode = 5
  Support = -> [XY_Plane010]
  sketch-geometry (1):
    g0: Circle CenterX=0 CenterY=0 CenterZ=0 NormalX=0 NormalY=0 NormalZ=1 AngleXU=0 Radius=1.5
  constraints (2):
    c: Coincident(g0,g-1)
    c: Diameter(g0) = 3
FEATURE [PartDesign::Pad] Pad013
  AllowMultiFace = false
  Direction = (1,1,1)
  Length = 10
  Length2 = 100
  Profile = -> Sketch028
  Type = 0
FEATURE [PartDesign::Chamfer] Chamfer003
  Angle = 45
  Base = -> Pad013 [Edge3]
  BaseFeature = -> Pad013
  ChamferType = 0
  FlipDirection = false
  Size = 1.4
  Size2 = 1
  SupportTransform = false
  UseAllEdges = false
FEATURE [PartDesign::Pocket] Pocket014
  AllowMultiFace = false
  BaseFeature = -> Chamfer003
  Direction = (1,1,1)
  Length = 1.5
  Length2 = 100
  Profile = -> Sketch027
  Reversed = true
  Type = 0
FEATURE [PartDesign::Chamfer] Chamfer002
  Angle = 45
  Base = -> Pocket014 [Edge3]
  BaseFeature = -> Pocket014
  ChamferType = 0
  FlipDirection = false
  Size = 0.1
  Size2 = 1
  SupportTransform = false
  UseAllEdges = false
FEATURE [PartDesign::Body] Body006  label="bodyVisPointeauM3x10_002"
  Group = -> [Sketch028,Pad013,Chamfer003,Sketch027,Pocket014,Chamfer002]
  Origin = -> Origin015
  Tip = -> Chamfer002
COMPONENT P15 — recipe-attached ("tigeLaiton001", modeled in this document).
Construction recipe (the document's own serialized feature program — sketch geometry with constraints, then the solid features built on it; lengths are millimeters unless a unit is written):

FEATURE [PartDesign::Plane] DatumPlane012  label="planBaseTige"
  AttachmentOffset = pos=(0,0,-5.18) rot=(0,0,1;0rad)
  Length = 60
  MapMode = 5
  Placement = pos=(-5.18,1.2e-15,-1.2e-15) rot=(0.57735,0.57735,0.57735;2.0944rad)
  ResizeMode = 0
  Support = -> [YZ_Plane012]
  Width = 60
  expr: .AttachmentOffset.Base.z = -<<tige>>.planBaseTigeposX
FEATURE [Sketcher::SketchObject] Sketch032  label="sk_tiges"
  FullyConstrained = true
  MapMode = 5
  Placement = pos=(-5.18,1.2e-15,-1.2e-15) rot=(0.57735,0.57735,0.57735;2.0944rad)
  Support = -> [DatumPlane012]
  expr: Constraints[0] = <<tige>>.tigeDiam
  expr: Constraints[1] = <<tige>>.tigePosY
  expr: Constraints[2] = <<tige>>.tigePosX
  sketch-geometry (1):
    g0: Circle CenterX=-14 CenterY=14.3 CenterZ=0 NormalX=0 NormalY=0 NormalZ=1 AngleXU=0 Radius=1.25
  constraints (3):
    c: Diameter(g0) = 2.5
    c: DistanceY(g-1,g0) = 14.3
    c: DistanceX(g0,g-1) = 14
FEATURE [PartDesign::Pad] Pad017  label="tigeBasse"
  AllowMultiFace = false
  Direction = (1,1,1)
  Length = 133.62
  Length2 = 100
  Placement = pos=(-5.18,1e-15,-1e-15) rot=(0.57735,0.57735,0.57735;2.0944rad)
  Profile = -> Sketch032
  Reversed = true
  Type = 0
  expr: Length = <<tige>>.tigeLong
FEATURE [PartDesign::Body] Body007  label="tigeLaiton"
  Group = -> [DatumPlane012,Sketch032,Pad017]
  Origin = -> Origin016
  Tip = -> Pad017
FEATURE [PartDesign::Plane] DatumPlane013  label="planTige2"
  AttachmentOffset = pos=(0,0,-5.18) rot=(0,0,1;0rad)
  Length = 60
  MapMode = 5
  Placement = pos=(-5.18,1.2e-15,-1.2e-15) rot=(0.57735,0.57735,0.57735;2.0944rad)
  ResizeMode = 0
  Support = -> [YZ_Plane014]
  Width = 60
  expr: .AttachmentOffset.Base.z = -<<tige>>.planBaseTigeposX
FEATURE [Sketcher::SketchObject] Sketch033  label="sk_tige2"
  FullyConstrained = true
  MapMode = 5
  Placement = pos=(-5.18,1.2e-15,-1.2e-15) rot=(0.57735,0.57735,0.57735;2.0944rad)
  Support = -> [DatumPlane013]
  expr: Constraints[0] = <<tige>>.tigeDiam
  expr: Constraints[1] = <<tige>>.tigePosX
  expr: Constraints[2] = <<tige>>.tigePosY + <<tige>>.xtEcartBroches
  sketch-geometry (1):
    g0: Circle CenterX=-14 CenterY=21.86 CenterZ=0 NormalX=0 NormalY=0 NormalZ=1 AngleXU=0 Radius=1.25
  constraints (3):
    c: Diameter(g0) = 2.5
    c: DistanceX(g0,g-1) = 14
    c: DistanceY(g-1,g0) = 21.86
FEATURE [PartDesign::Pad] Pad018
  AllowMultiFace = false
  Direction = (1,1,1)
  Length = 133.62
  Length2 = 100
  Placement = pos=(-5.18,1e-15,-1e-15) rot=(0.57735,0.57735,0.57735;2.0944rad)
  Profile = -> Sketch033
  Reversed = true
  Type = 0
  expr: Length = <<tige>>.tigeLong
FEATURE [PartDesign::Body] Body008  label="tige2"
  Group = -> [DatumPlane013,Sketch033,Pad018]
  Origin = -> Origin018
  Tip = -> Pad018
COMPONENT P16 — recipe-attached ("BNC_embase", modeled in this document).
Construction recipe (the document's own serialized feature program — sketch geometry with constraints, then the solid features built on it; lengths are millimeters unless a unit is written):

FEATURE [Sketcher::SketchObject] Sketch037  label="sk_trou"
  FullyConstrained = true
  MapMode = 5
  Support = -> [XY_Plane041]
  expr: Constraints[1] = <<bnc>>.trouDiam + <<bnc>>.trouJeu
  expr: Constraints[5] = <<bnc>>.trouMeplatDepuisLeCentre + <<bnc>>.trouJeu
  sketch-geometry (2):
    g0: ArcOfCircle CenterX=0 CenterY=0 CenterZ=0 NormalX=0 NormalY=0 NormalZ=1 AngleXU=0 Radius=5.15 StartAngle=0.696659 EndAngle=5.58653
    g1: LineSegment StartX=3.95 StartY=3.30454 StartZ=0 EndX=3.95 EndY=-3.30454 EndZ=0
  constraints (6):
    c: Coincident(g0,g-1)
    c: Diameter(g0) = 10.3
    c: Vertical(g1)
    c: Coincident(g0,g1)
    c: Coincident(g0,g1)
    c: DistanceX(g0,g0) = 3.95
FEATURE [PartDesign::Body] Body009  label="bncBodyPourTrou"
  Group = -> [Sketch037]
  Origin = -> Origin041
COMPONENT P17 — recipe-attached ("groupeDCDC", modeled in this document).
Construction recipe (the document's own serialized feature program — sketch geometry with constraints, then the solid features built on it; lengths are millimeters unless a unit is written):

FEATURE [Sketcher::SketchObject] Sketch041
  FullyConstrained = false
  MapMode = 5
  Support = -> [XY_Plane044]
  sketch-geometry (1):
    g0: Circle CenterX=0 CenterY=0 CenterZ=0 NormalX=0 NormalY=0 NormalZ=1 AngleXU=0 Radius=2.75
  constraints (2):
    c: Coincident(g0,g-1)
    c: Diameter(g0) = 5.5
FEATURE [PartDesign::Pad] Pad020  label="tete002"
  AllowMultiFace = false
  Direction = (1,1,1)
  Length = 3
  Length2 = 100
  Profile = -> Sketch041
  Type = 0
FEATURE [Sketcher::SketchObject] Sketch042
  FullyConstrained = false
  MapMode = 5
  Placement = pos=(0,0,0) rot=(1,0,0;3.14159rad)
  Support = -> [Pad020]
  sketch-geometry (1):
    g0: Circle CenterX=0 CenterY=0 CenterZ=0 NormalX=0 NormalY=0 NormalZ=1 AngleXU=0 Radius=1.5
  constraints (2):
    c: Coincident(g0,g-1)
    c: Diameter(g0) = 3
FEATURE [PartDesign::Pad] Pad021  label="corps002"
  AllowMultiFace = false
  BaseFeature = -> Pad020
  Direction = (1,1,1)
  Length = 6
  Length2 = 100
  Profile = -> Sketch042
  Type = 0
FEATURE [PartDesign::Plane] DatumPlane016
  AttachmentOffset = pos=(0,0,3) rot=(0,0,1;0rad)
  Length = 60
  MapMode = 5
  Placement = pos=(0,0,3) rot=(0,0,1;0rad)
  ResizeMode = 0
  Support = -> [XY_Plane044]
  Width = 60
FEATURE [Sketcher::SketchObject] Sketch043  label="Sketch002"
  FullyConstrained = false
  MapMode = 5
  Placement = pos=(0,0,3) rot=(0,0,1;0rad)
  Support = -> [DatumPlane016]
  sketch-geometry (7):
    g0: LineSegment StartX=0.721688 StartY=-1.25 StartZ=0 EndX=1.44338 EndY=1.0119e-12 EndZ=0
    g1: LineSegment StartX=1.44338 StartY=1.0119e-12 StartZ=0 EndX=0.721688 EndY=1.25 EndZ=0
    g2: LineSegment StartX=0.721688 StartY=1.25 StartZ=0 EndX=-0.721688 EndY=1.25 EndZ=0
    g3: LineSegment StartX=-0.721688 StartY=1.25 StartZ=0 EndX=-1.44338 EndY=8.689e-13 EndZ=0
    g4: LineSegment StartX=-1.44338 StartY=8.689e-13 StartZ=0 EndX=-0.721688 EndY=-1.25 EndZ=0
    g5: LineSegment StartX=-0.721688 StartY=-1.25 StartZ=0 EndX=0.721688 EndY=-1.25 EndZ=0
    g6: Circle CenterX=0 CenterY=0 CenterZ=0 NormalX=0 NormalY=0 NormalZ=1 AngleXU=0 Radius=1.44338
  constraints (16):
    c: Coincident(g0,g1)
    c: Coincident(g1,g2)
    c: Coincident(g2,g3)
    c: Coincident(g3,g4)
    c: Coincident(g4,g5)
    c: Coincident(g5,g0)
    c: Equal(g0, g1-g5) x5
    c: PointOnObject(g0,g6)
    c: PointOnObject(g1,g6)
    c: PointOnObject(g2,g6)
    c: PointOnObject(g3,g6)
    c: PointOnObject(g4,g6)
    c: PointOnObject(g5,g6)
    c: Coincident(g6,g-1)
    c: Horizontal(g2)
    c: DistanceY(g0,g1) = 2.5
FEATURE [PartDesign::Pocket] Pocket020  label="emprunte002"
  AllowMultiFace = false
  BaseFeature = -> Pad021
  Direction = (1,1,1)
  Length = 4
  Length2 = 100
  Profile = -> Sketch043
  Type = 0
FEATURE [PartDesign::Body] Body011  label="visTHCM3x6_DCDC001"
  Group = -> [Sketch041,Pad020,Sketch042,Pad021,DatumPlane016,Sketch043,Pocket020]
  Origin = -> Origin046
  Placement = pos=(-40.02,-40.03,10.89) rot=(0,0,1;0rad)
  Tip = -> Pocket020
FEATURE [Sketcher::SketchObject] Sketch046
  FullyConstrained = false
  MapMode = 5
  Support = -> [XY_Plane045]
  sketch-geometry (1):
    g0: Circle CenterX=0 CenterY=0 CenterZ=0 NormalX=0 NormalY=0 NormalZ=1 AngleXU=0 Radius=2.75
  constraints (2):
    c: Coincident(g0,g-1)
    c: Diameter(g0) = 5.5
FEATURE [PartDesign::Pad] Pad023  label="tete003"
  AllowMultiFace = false
  Direction = (1,1,1)
  Length = 3
  Length2 = 100
  Profile = -> Sketch046
  Type = 0
FEATURE [Sketcher::SketchObject] Sketch044
  FullyConstrained = false
  MapMode = 5
  Placement = pos=(0,0,0) rot=(1,0,0;3.14159rad)
  Support = -> [Pad023]
  sketch-geometry (1):
    g0: Circle CenterX=0 CenterY=0 CenterZ=0 NormalX=0 NormalY=0 NormalZ=1 AngleXU=0 Radius=1.5
  constraints (2):
    c: Coincident(g0,g-1)
    c: Diameter(g0) = 3
FEATURE [PartDesign::Pad] Pad022  label="corps003"
  AllowMultiFace = false
  BaseFeature = -> Pad023
  Direction = (1,1,1)
  Length = 6
  Length2 = 100
  Profile = -> Sketch044
  Type = 0
FEATURE [PartDesign::Plane] DatumPlane017
  AttachmentOffset = pos=(0,0,3) rot=(0,0,1;0rad)
  Length = 60
  MapMode = 5
  Placement = pos=(0,0,3) rot=(0,0,1;0rad)
  ResizeMode = 0
  Support = -> [XY_Plane045]
  Width = 60
FEATURE [Sketcher::SketchObject] Sketch045
  FullyConstrained = false
  MapMode = 5
  Placement = pos=(0,0,3) rot=(0,0,1;0rad)
  Support = -> [DatumPlane017]
  sketch-geometry (7):
    g0: LineSegment StartX=0.721688 StartY=-1.25 StartZ=0 EndX=1.44338 EndY=1.0119e-12 EndZ=0
    g1: LineSegment StartX=1.44338 StartY=1.0119e-12 StartZ=0 EndX=0.721688 EndY=1.25 EndZ=0
    g2: LineSegment StartX=0.721688 StartY=1.25 StartZ=0 EndX=-0.721688 EndY=1.25 EndZ=0
    g3: LineSegment StartX=-0.721688 StartY=1.25 StartZ=0 EndX=-1.44338 EndY=8.689e-13 EndZ=0
    g4: LineSegment StartX=-1.44338 StartY=8.689e-13 StartZ=0 EndX=-0.721688 EndY=-1.25 EndZ=0
    g5: LineSegment StartX=-0.721688 StartY=-1.25 StartZ=0 EndX=0.721688 EndY=-1.25 EndZ=0
    g6: Circle CenterX=0 CenterY=0 CenterZ=0 NormalX=0 NormalY=0 NormalZ=1 AngleXU=0 Radius=1.44338
  constraints (16):
    c: Coincident(g0,g1)
    c: Coincident(g1,g2)
    c: Coincident(g2,g3)
    c: Coincident(g3,g4)
    c: Coincident(g4,g5)
    c: Coincident(g5,g0)
    c: Equal(g0, g1-g5) x5
    c: PointOnObject(g0,g6)
    c: PointOnObject(g1,g6)
    c: PointOnObject(g2,g6)
    c: PointOnObject(g3,g6)
    c: PointOnObject(g4,g6)
    c: PointOnObject(g5,g6)
    c: Coincident(g6,g-1)
    c: Horizontal(g2)
    c: DistanceY(g0,g1) = 2.5
FEATURE [PartDesign::Pocket] Pocket021  label="emprunte003"
  AllowMultiFace = false
  BaseFeature = -> Pad022
  Direction = (1,1,1)
  Length = 4
  Length2 = 100
  Profile = -> Sketch045
  Type = 0
FEATURE [PartDesign::Body] Body012  label="visTHCM3x6_DCDC002"
  Group = -> [Sketch046,Pad023,Sketch044,Pad022,DatumPlane017,Sketch045,Pocket021]
  Origin = -> Origin047
  Placement = pos=(-71.22,-23.18,10.89) rot=(0,0,1;0rad)
  Tip = -> Pocket021
COMPONENT P18 — geometry summary ("switch"; no construction recipe available for this part):
  bounding box: 38.3 x 33.1 x 13.9 mm
  tessellated surface: 3,968 triangles
  volume: 6127 mm^3 (35% of its bounding box)
PROVENANCE & LICENSES
A FreeCAD (.FCStd) document from a public repository crawl; recipes are the document's own serialized feature recipes (and, for linked parts, companion documents' recipes).
License: as declared in the source repository (recorded in the dataset sidecar).
